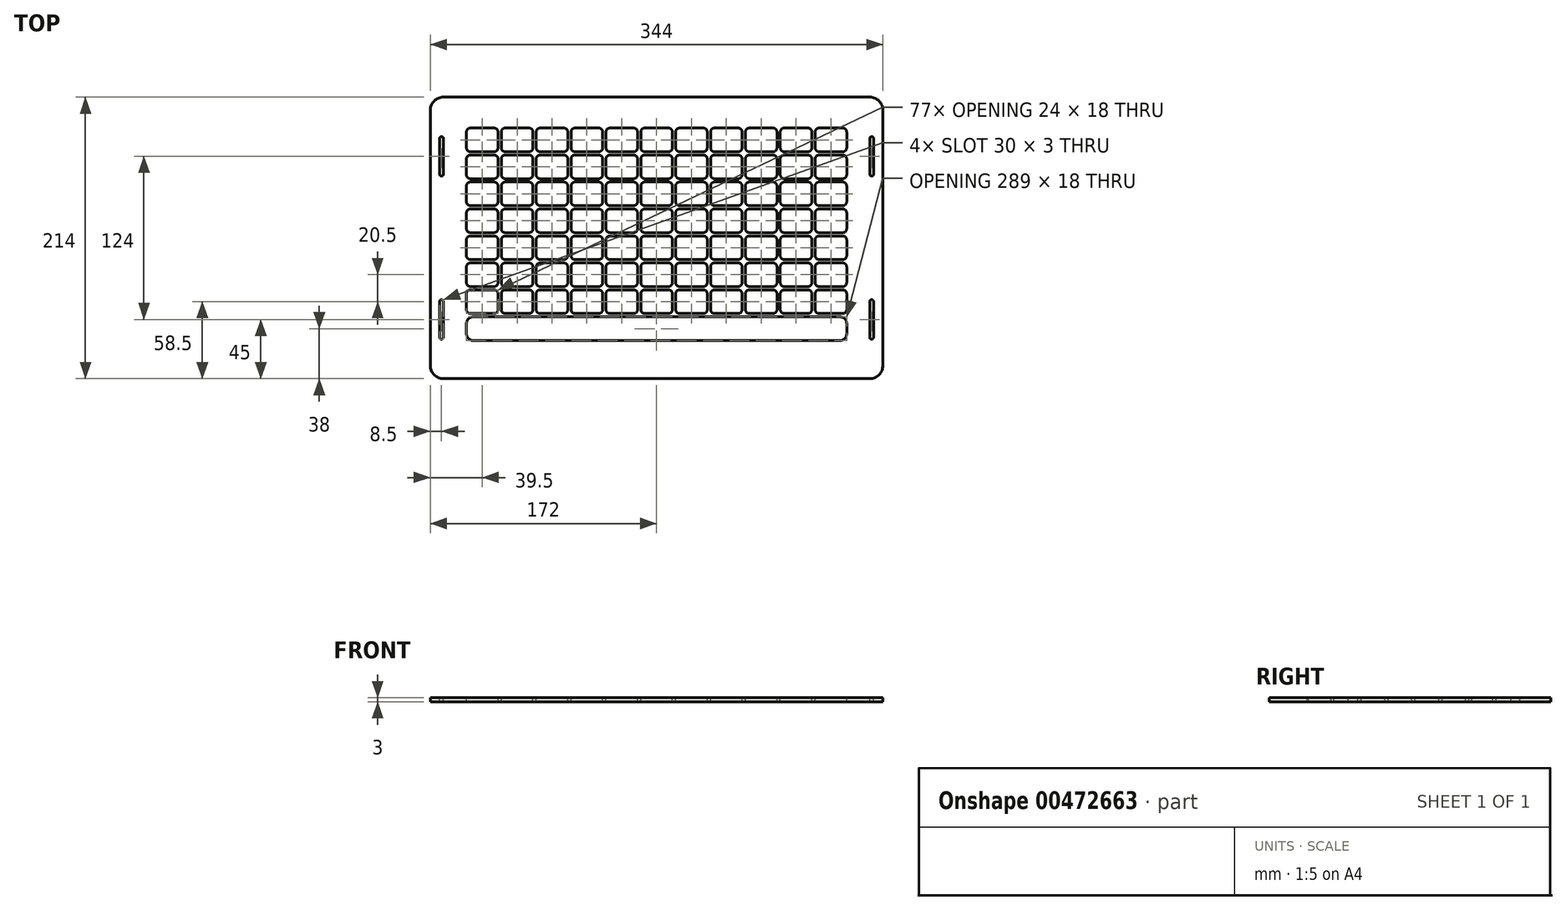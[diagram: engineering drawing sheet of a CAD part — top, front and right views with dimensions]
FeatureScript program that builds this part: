
annotation { "Feature Type Name" : "Feature", "Feature Type Description" : "" }
export const myFeature = defineFeature(function(context is Context, id is Id, definition is map)
    precondition{}
    {
        {
            var Q0;
            Q0=qCreatedBy(makeId("Top.planeOp"),FACE);
            var sketch = newSketch(context, id + "F0", { "sketchPlane" : qUnion([Q0])});
            skLineSegment(sketch, "E0.bottom", {"start": v(162, -107) * mm, "end": v(-162, -107) * mm});
            skLineSegment(sketch, "E0.top", {"start": v(162, 107) * mm, "end": v(-162, 107) * mm});
            skLineSegment(sketch, "E0.left", {"start": v(172, -97) * mm, "end": v(172, 97) * mm});
            skLineSegment(sketch, "E0.right", {"start": v(-172, -97) * mm, "end": v(-172, 97) * mm});
            skPoint(sketch, "E0.middle", {"position": v(0, 0) * mm});
            skPoint(sketch, "E1.visualSharp", {"position": v(-172, 107) * mm});
            skArc(sketch, "E1.filletArc", {"start": v(-162, 107) * mm, "mid": v(-169.07, 104.07) * mm, "end": v(-172, 97) * mm});
            skPoint(sketch, "E2.visualSharp", {"position": v(172, 107) * mm});
            skArc(sketch, "E2.filletArc", {"start": v(172, 97) * mm, "mid": v(169.07, 104.07) * mm, "end": v(162, 107) * mm});
            skPoint(sketch, "E3.visualSharp", {"position": v(172, -107) * mm});
            skArc(sketch, "E3.filletArc", {"start": v(162, -107) * mm, "mid": v(169.07, -104.07) * mm, "end": v(172, -97) * mm});
            skPoint(sketch, "E4.visualSharp", {"position": v(-172, -107) * mm});
            skArc(sketch, "E4.filletArc", {"start": v(-172, -97) * mm, "mid": v(-169.07, -104.07) * mm, "end": v(-162, -107) * mm});
            skSolve(sketch);
        }
        {
            var Q0;
            Q0 = qSketchRegion(id + "F0", true);
            extrude(context, id + "F1", {"entities" : qUnion([Q0]), "depth" : 3 * mm});
        }
        {
            var Q0;
            Q0=makeQuery(id+"F1.opExtrude","CAP_FACE",FACE,{"disambiguationData":[OSD([sQuery(id+"F0.wireOp",EDGE,"E0.bottom"),sQuery(id+"F0.wireOp",EDGE,"E0.top"),sQuery(id+"F0.wireOp",EDGE,"E0.left"),sQuery(id+"F0.wireOp",EDGE,"E0.right"),sQuery(id+"F0.wireOp",EDGE,"E1.filletArc"),sQuery(id+"F0.wireOp",EDGE,"E2.filletArc"),sQuery(id+"F0.wireOp",EDGE,"E3.filletArc"),sQuery(id+"F0.wireOp",EDGE,"E4.filletArc")])],"isStart":false});
            var sketch = newSketch(context, id + "F2", { "sketchPlane" : qUnion([Q0])});
            skLineSegment(sketch, "E5", {"start": v(-162, -47) * mm, "end": v(-162, -75.5) * mm});
            skLineSegment(sketch, "E6", {"start": v(0, 0) * mm, "end": v(72.85, 0) * mm, "construction": true});
            skLineSegment(sketch, "E7.bottom", {"start": v(-163.5, -77) * mm, "end": v(-163.5, -77) * mm});
            skLineSegment(sketch, "E7.top", {"start": v(-163.5, -47) * mm, "end": v(-163.5, -47) * mm});
            skLineSegment(sketch, "E7.left", {"start": v(-162, -77) * mm, "end": v(-162, -48.5) * mm});
            skLineSegment(sketch, "E7.right", {"start": v(-165, -75.5) * mm, "end": v(-165, -48.5) * mm});
            skPoint(sketch, "E8.visualSharp", {"position": v(-162, -47) * mm});
            skArc(sketch, "E8.filletArc", {"start": v(-162, -48.5) * mm, "mid": v(-162.44, -47.44) * mm, "end": v(-163.5, -47) * mm});
            skPoint(sketch, "E9.visualSharp", {"position": v(-165, -47) * mm});
            skArc(sketch, "E9.filletArc", {"start": v(-163.5, -47) * mm, "mid": v(-164.56, -47.44) * mm, "end": v(-165, -48.5) * mm});
            skPoint(sketch, "E10.visualSharp", {"position": v(-165, -77) * mm});
            skArc(sketch, "E10.filletArc", {"start": v(-165, -75.5) * mm, "mid": v(-164.56, -76.56) * mm, "end": v(-163.5, -77) * mm});
            skPoint(sketch, "E11.visualSharp", {"position": v(-162, -77) * mm});
            skArc(sketch, "E11.filletArc", {"start": v(-163.5, -77) * mm, "mid": v(-162.44, -76.56) * mm, "end": v(-162, -75.5) * mm});
            skPoint(sketch, "E12.end.orphan", {"position": v(-162, 77) * mm});
            skPoint(sketch, "E13.end.orphan", {"position": v(162, 77) * mm});
            skArc(sketch, "E14.MirrorCS", {"start": v(163.5, -77) * mm, "mid": v(162.44, -76.56) * mm, "end": v(162, -75.5) * mm});
            skArc(sketch, "E15.MirrorCS", {"start": v(165, -75.5) * mm, "mid": v(164.56, -76.56) * mm, "end": v(163.5, -77) * mm});
            skArc(sketch, "E16.MirrorCS", {"start": v(163.5, -47) * mm, "mid": v(164.56, -47.44) * mm, "end": v(165, -48.5) * mm});
            skArc(sketch, "E17.MirrorCS", {"start": v(162, -48.5) * mm, "mid": v(162.44, -47.44) * mm, "end": v(163.5, -47) * mm});
            skLineSegment(sketch, "E18.MirrorCS", {"start": v(162, -47) * mm, "end": v(162, -75.5) * mm});
            skLineSegment(sketch, "E19.MirrorCS", {"start": v(163.5, -77) * mm, "end": v(163.5, -77) * mm});
            skPoint(sketch, "E20.MirrorP", {"position": v(162, -47) * mm});
            skLineSegment(sketch, "E21.MirrorCS", {"start": v(163.5, -47) * mm, "end": v(163.5, -47) * mm});
            skLineSegment(sketch, "E22.MirrorCS", {"start": v(162, -77) * mm, "end": v(162, -48.5) * mm});
            skLineSegment(sketch, "E23.MirrorCS", {"start": v(165, -75.5) * mm, "end": v(165, -48.5) * mm});
            skPoint(sketch, "E24.MirrorP", {"position": v(165, -77) * mm});
            skPoint(sketch, "E25.MirrorP", {"position": v(165, -47) * mm});
            skPoint(sketch, "E26.MirrorP", {"position": v(162, -77) * mm});
            skArc(sketch, "E27.MirrorCS", {"start": v(-165, 75.5) * mm, "mid": v(-164.56, 76.56) * mm, "end": v(-163.5, 77) * mm});
            skArc(sketch, "E28.MirrorCS", {"start": v(-163.5, 77) * mm, "mid": v(-162.44, 76.56) * mm, "end": v(-162, 75.5) * mm});
            skArc(sketch, "E29.MirrorCS", {"start": v(165, 75.5) * mm, "mid": v(164.56, 76.56) * mm, "end": v(163.5, 77) * mm});
            skArc(sketch, "E30.MirrorCS", {"start": v(-162, 48.5) * mm, "mid": v(-162.44, 47.44) * mm, "end": v(-163.5, 47) * mm});
            skArc(sketch, "E31.MirrorCS", {"start": v(-163.5, 47) * mm, "mid": v(-164.56, 47.44) * mm, "end": v(-165, 48.5) * mm});
            skArc(sketch, "E32.MirrorCS", {"start": v(163.5, 77) * mm, "mid": v(162.44, 76.56) * mm, "end": v(162, 75.5) * mm});
            skArc(sketch, "E33.MirrorCS", {"start": v(163.5, 47) * mm, "mid": v(164.56, 47.44) * mm, "end": v(165, 48.5) * mm});
            skArc(sketch, "E34.MirrorCS", {"start": v(162, 48.5) * mm, "mid": v(162.44, 47.44) * mm, "end": v(163.5, 47) * mm});
            skLineSegment(sketch, "E35.MirrorCS", {"start": v(162, 47) * mm, "end": v(162, 75.5) * mm});
            skLineSegment(sketch, "E36.MirrorCS", {"start": v(-162, 47) * mm, "end": v(-162, 75.5) * mm});
            skPoint(sketch, "E37.MirrorP", {"position": v(162, 47) * mm});
            skLineSegment(sketch, "E38.MirrorCS", {"start": v(-162, 77) * mm, "end": v(-162, 48.5) * mm});
            skLineSegment(sketch, "E39.MirrorCS", {"start": v(-165, 75.5) * mm, "end": v(-165, 48.5) * mm});
            skLineSegment(sketch, "E40.MirrorCS", {"start": v(163.5, 47) * mm, "end": v(163.5, 47) * mm});
            skPoint(sketch, "E41.MirrorP", {"position": v(165, 77) * mm});
            skPoint(sketch, "E42.MirrorP", {"position": v(-165, 77) * mm});
            skPoint(sketch, "E43.MirrorP", {"position": v(165, 47) * mm});
            skLineSegment(sketch, "E44.MirrorCS", {"start": v(-163.5, 47) * mm, "end": v(-163.5, 47) * mm});
            skPoint(sketch, "E45.MirrorP", {"position": v(-162, 47) * mm});
            skLineSegment(sketch, "E46.MirrorCS", {"start": v(162, 77) * mm, "end": v(162, 48.5) * mm});
            skPoint(sketch, "E47.MirrorP", {"position": v(-165, 47) * mm});
            skLineSegment(sketch, "E48.MirrorCS", {"start": v(165, 75.5) * mm, "end": v(165, 48.5) * mm});
            skLineSegment(sketch, "E49.MirrorCS", {"start": v(163.5, 77) * mm, "end": v(163.5, 77) * mm});
            skLineSegment(sketch, "E50.MirrorCS", {"start": v(-163.5, 77) * mm, "end": v(-163.5, 77) * mm});
            skSolve(sketch);
        }
        {
            var Q0;
            Q0 = qSketchRegion(id + "F2", true);
            extrude(context, id + "F3", {"entities" : qUnion([Q0]), "operationType" : NewBodyOperationType.REMOVE, "oppositeDirection" : true, "depth" : 3 * mm});
        }
        {
            var Q0;
            Q0=makeQuery(id+"F1.opExtrude","CAP_FACE",FACE,{"disambiguationData":[OSD([sQuery(id+"F0.wireOp",EDGE,"E0.bottom"),sQuery(id+"F0.wireOp",EDGE,"E0.top"),sQuery(id+"F0.wireOp",EDGE,"E0.left"),sQuery(id+"F0.wireOp",EDGE,"E0.right"),sQuery(id+"F0.wireOp",EDGE,"E1.filletArc"),sQuery(id+"F0.wireOp",EDGE,"E2.filletArc"),sQuery(id+"F0.wireOp",EDGE,"E3.filletArc"),sQuery(id+"F0.wireOp",EDGE,"E4.filletArc")])],"isStart":false});
            var sketch = newSketch(context, id + "F4", { "sketchPlane" : qUnion([Q0])});
            skLineSegment(sketch, "E51.top", {"start": v(-9, 4) * mm, "end": v(9, 4) * mm});
            skLineSegment(sketch, "E51.left", {"start": v(-12, 19) * mm, "end": v(-12, 7) * mm});
            skLineSegment(sketch, "E51.right", {"start": v(12, 19) * mm, "end": v(12, 7) * mm});
            skPoint(sketch, "E51.middle", {"position": v(0, 13) * mm});
            skPoint(sketch, "E52.visualSharp", {"position": v(-12, 22) * mm});
            skArc(sketch, "E52.filletArc", {"start": v(-9, 22) * mm, "mid": v(-11.12, 21.12) * mm, "end": v(-12, 19) * mm});
            skPoint(sketch, "E53.visualSharp", {"position": v(12, 22) * mm});
            skArc(sketch, "E53.filletArc", {"start": v(12, 19) * mm, "mid": v(11.12, 21.12) * mm, "end": v(9, 22) * mm});
            skPoint(sketch, "E54.visualSharp", {"position": v(12, 4) * mm});
            skArc(sketch, "E54.filletArc", {"start": v(9, 4) * mm, "mid": v(11.12, 4.88) * mm, "end": v(12, 7) * mm});
            skPoint(sketch, "E55.visualSharp", {"position": v(-12, 4) * mm});
            skArc(sketch, "E55.filletArc", {"start": v(-12, 7) * mm, "mid": v(-11.12, 4.88) * mm, "end": v(-9, 4) * mm});
            skPoint(sketch, "E56.1.0.0", {"position": v(14.5, 4) * mm});
            skPoint(sketch, "E56.1.0.1", {"position": v(38.5, 4) * mm});
            skPoint(sketch, "E56.1.0.2", {"position": v(26.5, 13) * mm});
            skLineSegment(sketch, "E56.1.0.3", {"start": v(38.5, 19) * mm, "end": v(38.5, 7) * mm});
            skLineSegment(sketch, "E56.1.0.4", {"start": v(14.5, 19) * mm, "end": v(14.5, 7) * mm});
            skPoint(sketch, "E56.1.0.5", {"position": v(38.5, 22) * mm});
            skPoint(sketch, "E56.1.0.6", {"position": v(14.5, 22) * mm});
            skLineSegment(sketch, "E56.1.0.7", {"start": v(17.5, 22) * mm, "end": v(35.5, 22) * mm});
            skLineSegment(sketch, "E56.1.0.8", {"start": v(17.5, 4) * mm, "end": v(35.5, 4) * mm});
            skArc(sketch, "E56.1.0.9", {"start": v(14.5, 7) * mm, "mid": v(15.38, 4.88) * mm, "end": v(17.5, 4) * mm});
            skArc(sketch, "E56.1.0.10", {"start": v(35.5, 4) * mm, "mid": v(37.62, 4.88) * mm, "end": v(38.5, 7) * mm});
            skArc(sketch, "E56.1.0.11", {"start": v(38.5, 19) * mm, "mid": v(37.62, 21.12) * mm, "end": v(35.5, 22) * mm});
            skArc(sketch, "E56.1.0.12", {"start": v(17.5, 22) * mm, "mid": v(15.38, 21.12) * mm, "end": v(14.5, 19) * mm});
            skPoint(sketch, "E56.2.0.0", {"position": v(41, 4) * mm});
            skPoint(sketch, "E56.2.0.1", {"position": v(65, 4) * mm});
            skPoint(sketch, "E56.2.0.2", {"position": v(53, 13) * mm});
            skLineSegment(sketch, "E56.2.0.3", {"start": v(65, 19) * mm, "end": v(65, 7) * mm});
            skLineSegment(sketch, "E56.2.0.4", {"start": v(41, 19) * mm, "end": v(41, 7) * mm});
            skPoint(sketch, "E56.2.0.5", {"position": v(65, 22) * mm});
            skPoint(sketch, "E56.2.0.6", {"position": v(41, 22) * mm});
            skLineSegment(sketch, "E56.2.0.7", {"start": v(44, 22) * mm, "end": v(62, 22) * mm});
            skLineSegment(sketch, "E56.2.0.8", {"start": v(44, 4) * mm, "end": v(62, 4) * mm});
            skArc(sketch, "E56.2.0.9", {"start": v(41, 7) * mm, "mid": v(41.88, 4.88) * mm, "end": v(44, 4) * mm});
            skArc(sketch, "E56.2.0.10", {"start": v(62, 4) * mm, "mid": v(64.12, 4.88) * mm, "end": v(65, 7) * mm});
            skArc(sketch, "E56.2.0.11", {"start": v(65, 19) * mm, "mid": v(64.12, 21.12) * mm, "end": v(62, 22) * mm});
            skArc(sketch, "E56.2.0.12", {"start": v(44, 22) * mm, "mid": v(41.88, 21.12) * mm, "end": v(41, 19) * mm});
            skPoint(sketch, "E56.3.0.0", {"position": v(67.5, 4) * mm});
            skPoint(sketch, "E56.3.0.1", {"position": v(91.5, 4) * mm});
            skPoint(sketch, "E56.3.0.2", {"position": v(79.5, 13) * mm});
            skLineSegment(sketch, "E56.3.0.3", {"start": v(91.5, 19) * mm, "end": v(91.5, 7) * mm});
            skLineSegment(sketch, "E56.3.0.4", {"start": v(67.5, 19) * mm, "end": v(67.5, 7) * mm});
            skPoint(sketch, "E56.3.0.5", {"position": v(91.5, 22) * mm});
            skPoint(sketch, "E56.3.0.6", {"position": v(67.5, 22) * mm});
            skLineSegment(sketch, "E56.3.0.7", {"start": v(70.5, 22) * mm, "end": v(88.5, 22) * mm});
            skLineSegment(sketch, "E56.3.0.8", {"start": v(70.5, 4) * mm, "end": v(88.5, 4) * mm});
            skArc(sketch, "E56.3.0.9", {"start": v(67.5, 7) * mm, "mid": v(68.38, 4.88) * mm, "end": v(70.5, 4) * mm});
            skArc(sketch, "E56.3.0.10", {"start": v(88.5, 4) * mm, "mid": v(90.62, 4.88) * mm, "end": v(91.5, 7) * mm});
            skArc(sketch, "E56.3.0.11", {"start": v(91.5, 19) * mm, "mid": v(90.62, 21.12) * mm, "end": v(88.5, 22) * mm});
            skArc(sketch, "E56.3.0.12", {"start": v(70.5, 22) * mm, "mid": v(68.38, 21.12) * mm, "end": v(67.5, 19) * mm});
            skPoint(sketch, "E56.4.0.0", {"position": v(94, 4) * mm});
            skPoint(sketch, "E56.4.0.1", {"position": v(118, 4) * mm});
            skPoint(sketch, "E56.4.0.2", {"position": v(106, 13) * mm});
            skLineSegment(sketch, "E56.4.0.3", {"start": v(118, 19) * mm, "end": v(118, 7) * mm});
            skLineSegment(sketch, "E56.4.0.4", {"start": v(94, 19) * mm, "end": v(94, 7) * mm});
            skPoint(sketch, "E56.4.0.5", {"position": v(118, 22) * mm});
            skPoint(sketch, "E56.4.0.6", {"position": v(94, 22) * mm});
            skLineSegment(sketch, "E56.4.0.7", {"start": v(97, 22) * mm, "end": v(115, 22) * mm});
            skLineSegment(sketch, "E56.4.0.8", {"start": v(97, 4) * mm, "end": v(115, 4) * mm});
            skArc(sketch, "E56.4.0.9", {"start": v(94, 7) * mm, "mid": v(94.88, 4.88) * mm, "end": v(97, 4) * mm});
            skArc(sketch, "E56.4.0.10", {"start": v(115, 4) * mm, "mid": v(117.12, 4.88) * mm, "end": v(118, 7) * mm});
            skArc(sketch, "E56.4.0.11", {"start": v(118, 19) * mm, "mid": v(117.12, 21.12) * mm, "end": v(115, 22) * mm});
            skArc(sketch, "E56.4.0.12", {"start": v(97, 22) * mm, "mid": v(94.88, 21.12) * mm, "end": v(94, 19) * mm});
            skPoint(sketch, "E56.5.0.0", {"position": v(120.5, 4) * mm});
            skPoint(sketch, "E56.5.0.1", {"position": v(144.5, 4) * mm});
            skPoint(sketch, "E56.5.0.2", {"position": v(132.5, 13) * mm});
            skLineSegment(sketch, "E56.5.0.3", {"start": v(144.5, 19) * mm, "end": v(144.5, 7) * mm});
            skLineSegment(sketch, "E56.5.0.4", {"start": v(120.5, 19) * mm, "end": v(120.5, 7) * mm});
            skPoint(sketch, "E56.5.0.5", {"position": v(144.5, 22) * mm});
            skPoint(sketch, "E56.5.0.6", {"position": v(120.5, 22) * mm});
            skLineSegment(sketch, "E56.5.0.7", {"start": v(123.5, 22) * mm, "end": v(141.5, 22) * mm});
            skLineSegment(sketch, "E56.5.0.8", {"start": v(123.5, 4) * mm, "end": v(141.5, 4) * mm});
            skArc(sketch, "E56.5.0.9", {"start": v(120.5, 7) * mm, "mid": v(121.38, 4.88) * mm, "end": v(123.5, 4) * mm});
            skArc(sketch, "E56.5.0.10", {"start": v(141.5, 4) * mm, "mid": v(143.62, 4.88) * mm, "end": v(144.5, 7) * mm});
            skArc(sketch, "E56.5.0.11", {"start": v(144.5, 19) * mm, "mid": v(143.62, 21.12) * mm, "end": v(141.5, 22) * mm});
            skArc(sketch, "E56.5.0.12", {"start": v(123.5, 22) * mm, "mid": v(121.38, 21.12) * mm, "end": v(120.5, 19) * mm});
            skLineSegment(sketch, "E56.direction1", {"start": v(-12, 4) * mm, "end": v(14.5, 4) * mm, "construction": true});
            skLineSegment(sketch, "E57.1.0.0", {"start": v(-14.5, 19) * mm, "end": v(-14.5, 7) * mm});
            skLineSegment(sketch, "E57.1.0.1", {"start": v(-38.5, 19) * mm, "end": v(-38.5, 7) * mm});
            skLineSegment(sketch, "E57.1.0.2", {"start": v(-35.5, 4) * mm, "end": v(-17.5, 4) * mm});
            skLineSegment(sketch, "E57.1.0.3", {"start": v(-35.5, 22) * mm, "end": v(-17.5, 22) * mm});
            skPoint(sketch, "E57.1.0.4", {"position": v(-38.5, 22) * mm});
            skPoint(sketch, "E57.1.0.5", {"position": v(-26.5, 13) * mm});
            skPoint(sketch, "E57.1.0.6", {"position": v(-38.5, 4) * mm});
            skPoint(sketch, "E57.1.0.7", {"position": v(-14.5, 4) * mm});
            skPoint(sketch, "E57.1.0.8", {"position": v(-14.5, 22) * mm});
            skArc(sketch, "E57.1.0.9", {"start": v(-17.5, 4) * mm, "mid": v(-15.38, 4.88) * mm, "end": v(-14.5, 7) * mm});
            skArc(sketch, "E57.1.0.10", {"start": v(-14.5, 19) * mm, "mid": v(-15.38, 21.12) * mm, "end": v(-17.5, 22) * mm});
            skArc(sketch, "E57.1.0.11", {"start": v(-35.5, 22) * mm, "mid": v(-37.62, 21.12) * mm, "end": v(-38.5, 19) * mm});
            skArc(sketch, "E57.1.0.12", {"start": v(-38.5, 7) * mm, "mid": v(-37.62, 4.88) * mm, "end": v(-35.5, 4) * mm});
            skLineSegment(sketch, "E57.2.0.0", {"start": v(-41, 19) * mm, "end": v(-41, 7) * mm});
            skLineSegment(sketch, "E57.2.0.1", {"start": v(-65, 19) * mm, "end": v(-65, 7) * mm});
            skLineSegment(sketch, "E57.2.0.2", {"start": v(-62, 4) * mm, "end": v(-44, 4) * mm});
            skLineSegment(sketch, "E57.2.0.3", {"start": v(-62, 22) * mm, "end": v(-44, 22) * mm});
            skPoint(sketch, "E57.2.0.4", {"position": v(-65, 22) * mm});
            skPoint(sketch, "E57.2.0.5", {"position": v(-53, 13) * mm});
            skPoint(sketch, "E57.2.0.6", {"position": v(-65, 4) * mm});
            skPoint(sketch, "E57.2.0.7", {"position": v(-41, 4) * mm});
            skPoint(sketch, "E57.2.0.8", {"position": v(-41, 22) * mm});
            skArc(sketch, "E57.2.0.9", {"start": v(-44, 4) * mm, "mid": v(-41.88, 4.88) * mm, "end": v(-41, 7) * mm});
            skArc(sketch, "E57.2.0.10", {"start": v(-41, 19) * mm, "mid": v(-41.88, 21.12) * mm, "end": v(-44, 22) * mm});
            skArc(sketch, "E57.2.0.11", {"start": v(-62, 22) * mm, "mid": v(-64.12, 21.12) * mm, "end": v(-65, 19) * mm});
            skArc(sketch, "E57.2.0.12", {"start": v(-65, 7) * mm, "mid": v(-64.12, 4.88) * mm, "end": v(-62, 4) * mm});
            skLineSegment(sketch, "E57.3.0.0", {"start": v(-67.5, 19) * mm, "end": v(-67.5, 7) * mm});
            skLineSegment(sketch, "E57.3.0.1", {"start": v(-91.5, 19) * mm, "end": v(-91.5, 7) * mm});
            skLineSegment(sketch, "E57.3.0.2", {"start": v(-88.5, 4) * mm, "end": v(-70.5, 4) * mm});
            skLineSegment(sketch, "E57.3.0.3", {"start": v(-88.5, 22) * mm, "end": v(-70.5, 22) * mm});
            skPoint(sketch, "E57.3.0.4", {"position": v(-91.5, 22) * mm});
            skPoint(sketch, "E57.3.0.5", {"position": v(-79.5, 13) * mm});
            skPoint(sketch, "E57.3.0.6", {"position": v(-91.5, 4) * mm});
            skPoint(sketch, "E57.3.0.7", {"position": v(-67.5, 4) * mm});
            skPoint(sketch, "E57.3.0.8", {"position": v(-67.5, 22) * mm});
            skArc(sketch, "E57.3.0.9", {"start": v(-70.5, 4) * mm, "mid": v(-68.38, 4.88) * mm, "end": v(-67.5, 7) * mm});
            skArc(sketch, "E57.3.0.10", {"start": v(-67.5, 19) * mm, "mid": v(-68.38, 21.12) * mm, "end": v(-70.5, 22) * mm});
            skArc(sketch, "E57.3.0.11", {"start": v(-88.5, 22) * mm, "mid": v(-90.62, 21.12) * mm, "end": v(-91.5, 19) * mm});
            skArc(sketch, "E57.3.0.12", {"start": v(-91.5, 7) * mm, "mid": v(-90.62, 4.88) * mm, "end": v(-88.5, 4) * mm});
            skLineSegment(sketch, "E57.4.0.0", {"start": v(-94, 19) * mm, "end": v(-94, 7) * mm});
            skLineSegment(sketch, "E57.4.0.1", {"start": v(-118, 19) * mm, "end": v(-118, 7) * mm});
            skLineSegment(sketch, "E57.4.0.2", {"start": v(-115, 4) * mm, "end": v(-97, 4) * mm});
            skLineSegment(sketch, "E57.4.0.3", {"start": v(-115, 22) * mm, "end": v(-97, 22) * mm});
            skPoint(sketch, "E57.4.0.4", {"position": v(-118, 22) * mm});
            skPoint(sketch, "E57.4.0.5", {"position": v(-106, 13) * mm});
            skPoint(sketch, "E57.4.0.6", {"position": v(-118, 4) * mm});
            skPoint(sketch, "E57.4.0.7", {"position": v(-94, 4) * mm});
            skPoint(sketch, "E57.4.0.8", {"position": v(-94, 22) * mm});
            skArc(sketch, "E57.4.0.9", {"start": v(-97, 4) * mm, "mid": v(-94.88, 4.88) * mm, "end": v(-94, 7) * mm});
            skArc(sketch, "E57.4.0.10", {"start": v(-94, 19) * mm, "mid": v(-94.88, 21.12) * mm, "end": v(-97, 22) * mm});
            skArc(sketch, "E57.4.0.11", {"start": v(-115, 22) * mm, "mid": v(-117.12, 21.12) * mm, "end": v(-118, 19) * mm});
            skArc(sketch, "E57.4.0.12", {"start": v(-118, 7) * mm, "mid": v(-117.12, 4.88) * mm, "end": v(-115, 4) * mm});
            skLineSegment(sketch, "E57.5.0.0", {"start": v(-120.5, 19) * mm, "end": v(-120.5, 7) * mm});
            skLineSegment(sketch, "E57.5.0.1", {"start": v(-144.5, 19) * mm, "end": v(-144.5, 7) * mm});
            skLineSegment(sketch, "E57.5.0.2", {"start": v(-141.5, 4) * mm, "end": v(-123.5, 4) * mm});
            skLineSegment(sketch, "E57.5.0.3", {"start": v(-141.5, 22) * mm, "end": v(-123.5, 22) * mm});
            skPoint(sketch, "E57.5.0.4", {"position": v(-144.5, 22) * mm});
            skPoint(sketch, "E57.5.0.5", {"position": v(-132.5, 13) * mm});
            skPoint(sketch, "E57.5.0.6", {"position": v(-144.5, 4) * mm});
            skPoint(sketch, "E57.5.0.7", {"position": v(-120.5, 4) * mm});
            skPoint(sketch, "E57.5.0.8", {"position": v(-120.5, 22) * mm});
            skArc(sketch, "E57.5.0.9", {"start": v(-123.5, 4) * mm, "mid": v(-121.38, 4.88) * mm, "end": v(-120.5, 7) * mm});
            skArc(sketch, "E57.5.0.10", {"start": v(-120.5, 19) * mm, "mid": v(-121.38, 21.12) * mm, "end": v(-123.5, 22) * mm});
            skArc(sketch, "E57.5.0.11", {"start": v(-141.5, 22) * mm, "mid": v(-143.62, 21.12) * mm, "end": v(-144.5, 19) * mm});
            skArc(sketch, "E57.5.0.12", {"start": v(-144.5, 7) * mm, "mid": v(-143.62, 4.88) * mm, "end": v(-141.5, 4) * mm});
            skLineSegment(sketch, "E57.direction1", {"start": v(-12, 4) * mm, "end": v(-38.5, 4) * mm, "construction": true});
            skPoint(sketch, "E58.0.1.0", {"position": v(41, 42.5) * mm});
            skPoint(sketch, "E58.0.1.1", {"position": v(106, 33.5) * mm});
            skPoint(sketch, "E58.0.1.2", {"position": v(-38.5, 42.5) * mm});
            skLineSegment(sketch, "E58.0.1.3", {"start": v(-9, 42.5) * mm, "end": v(9, 42.5) * mm});
            skPoint(sketch, "E58.0.1.5", {"position": v(-94, 42.5) * mm});
            skPoint(sketch, "E58.0.1.6", {"position": v(65, 42.5) * mm});
            skPoint(sketch, "E58.0.1.7", {"position": v(118, 24.5) * mm});
            skPoint(sketch, "E58.0.1.8", {"position": v(12, 24.5) * mm});
            skPoint(sketch, "E58.0.1.9", {"position": v(-94, 24.5) * mm});
            skPoint(sketch, "E58.0.1.10", {"position": v(53, 33.5) * mm});
            skPoint(sketch, "E58.0.1.11", {"position": v(94, 24.5) * mm});
            skPoint(sketch, "E58.0.1.12", {"position": v(65, 24.5) * mm});
            skPoint(sketch, "E58.0.1.13", {"position": v(-118, 24.5) * mm});
            skPoint(sketch, "E58.0.1.14", {"position": v(-41, 42.5) * mm});
            skPoint(sketch, "E58.0.1.15", {"position": v(12, 42.5) * mm});
            skLineSegment(sketch, "E58.0.1.16", {"start": v(-62, 42.5) * mm, "end": v(-44, 42.5) * mm});
            skLineSegment(sketch, "E58.0.1.17", {"start": v(-115, 42.5) * mm, "end": v(-97, 42.5) * mm});
            skPoint(sketch, "E58.0.1.18", {"position": v(-106, 33.5) * mm});
            skPoint(sketch, "E58.0.1.19", {"position": v(41, 24.5) * mm});
            skPoint(sketch, "E58.0.1.20", {"position": v(-41, 24.5) * mm});
            skLineSegment(sketch, "E58.0.1.21", {"start": v(17.5, 24.5) * mm, "end": v(35.5, 24.5) * mm});
            skPoint(sketch, "E58.0.1.22", {"position": v(-118, 42.5) * mm});
            skPoint(sketch, "E58.0.1.23", {"position": v(120.5, 42.5) * mm});
            skPoint(sketch, "E58.0.1.24", {"position": v(-65, 24.5) * mm});
            skPoint(sketch, "E58.0.1.25", {"position": v(-12, 42.5) * mm});
            skPoint(sketch, "E58.0.1.26", {"position": v(67.5, 24.5) * mm});
            skPoint(sketch, "E58.0.1.27", {"position": v(26.5, 33.5) * mm});
            skPoint(sketch, "E58.0.1.28", {"position": v(118, 42.5) * mm});
            skPoint(sketch, "E58.0.1.29", {"position": v(-12, 24.5) * mm});
            skPoint(sketch, "E58.0.1.30", {"position": v(-26.5, 33.5) * mm});
            skPoint(sketch, "E58.0.1.31", {"position": v(94, 42.5) * mm});
            skPoint(sketch, "E58.0.1.32", {"position": v(-91.5, 42.5) * mm});
            skPoint(sketch, "E58.0.1.33", {"position": v(-38.5, 24.5) * mm});
            skLineSegment(sketch, "E58.0.1.34", {"start": v(44, 42.5) * mm, "end": v(62, 42.5) * mm});
            skLineSegment(sketch, "E58.0.1.35", {"start": v(97, 42.5) * mm, "end": v(115, 42.5) * mm});
            skPoint(sketch, "E58.0.1.36", {"position": v(144.5, 24.5) * mm});
            skPoint(sketch, "E58.0.1.37", {"position": v(91.5, 42.5) * mm});
            skPoint(sketch, "E58.0.1.38", {"position": v(14.5, 24.5) * mm});
            skPoint(sketch, "E58.0.1.39", {"position": v(-79.5, 33.5) * mm});
            skPoint(sketch, "E58.0.1.40", {"position": v(-14.5, 24.5) * mm});
            skLineSegment(sketch, "E58.0.1.41", {"start": v(97, 24.5) * mm, "end": v(115, 24.5) * mm});
            skPoint(sketch, "E58.0.1.42", {"position": v(-120.5, 42.5) * mm});
            skLineSegment(sketch, "E58.0.1.43", {"start": v(-141.5, 24.5) * mm, "end": v(-123.5, 24.5) * mm});
            skLineSegment(sketch, "E58.0.1.44", {"start": v(44, 24.5) * mm, "end": v(62, 24.5) * mm});
            skLineSegment(sketch, "E58.0.1.45", {"start": v(-88.5, 24.5) * mm, "end": v(-70.5, 24.5) * mm});
            skPoint(sketch, "E58.0.1.46", {"position": v(91.5, 24.5) * mm});
            skPoint(sketch, "E58.0.1.47", {"position": v(38.5, 42.5) * mm});
            skPoint(sketch, "E58.0.1.48", {"position": v(-67.5, 42.5) * mm});
            skPoint(sketch, "E58.0.1.49", {"position": v(-144.5, 24.5) * mm});
            skPoint(sketch, "E58.0.1.50", {"position": v(38.5, 24.5) * mm});
            skPoint(sketch, "E58.0.1.51", {"position": v(-91.5, 24.5) * mm});
            skPoint(sketch, "E58.0.1.52", {"position": v(-144.5, 42.5) * mm});
            skPoint(sketch, "E58.0.1.53", {"position": v(-14.5, 42.5) * mm});
            skLineSegment(sketch, "E58.0.1.54", {"start": v(-35.5, 42.5) * mm, "end": v(-17.5, 42.5) * mm});
            skLineSegment(sketch, "E58.0.1.55", {"start": v(-141.5, 42.5) * mm, "end": v(-123.5, 42.5) * mm});
            skPoint(sketch, "E58.0.1.56", {"position": v(-65, 42.5) * mm});
            skLineSegment(sketch, "E58.0.1.57", {"start": v(-88.5, 42.5) * mm, "end": v(-70.5, 42.5) * mm});
            skPoint(sketch, "E58.0.1.58", {"position": v(67.5, 42.5) * mm});
            skPoint(sketch, "E58.0.1.59", {"position": v(132.5, 33.5) * mm});
            skLineSegment(sketch, "E58.0.1.60", {"start": v(-12, 24.5) * mm, "end": v(-38.5, 24.5) * mm, "construction": true});
            skLineSegment(sketch, "E58.0.1.61", {"start": v(17.5, 42.5) * mm, "end": v(35.5, 42.5) * mm});
            skPoint(sketch, "E58.0.1.62", {"position": v(79.5, 33.5) * mm});
            skPoint(sketch, "E58.0.1.63", {"position": v(14.5, 42.5) * mm});
            skPoint(sketch, "E58.0.1.64", {"position": v(-120.5, 24.5) * mm});
            skPoint(sketch, "E58.0.1.65", {"position": v(-132.5, 33.5) * mm});
            skPoint(sketch, "E58.0.1.66", {"position": v(-67.5, 24.5) * mm});
            skPoint(sketch, "E58.0.1.67", {"position": v(0, 33.5) * mm});
            skPoint(sketch, "E58.0.1.68", {"position": v(120.5, 24.5) * mm});
            skLineSegment(sketch, "E58.0.1.69", {"start": v(70.5, 42.5) * mm, "end": v(88.5, 42.5) * mm});
            skLineSegment(sketch, "E58.0.1.70", {"start": v(123.5, 42.5) * mm, "end": v(141.5, 42.5) * mm});
            skLineSegment(sketch, "E58.0.1.71", {"start": v(70.5, 24.5) * mm, "end": v(88.5, 24.5) * mm});
            skLineSegment(sketch, "E58.0.1.72", {"start": v(123.5, 24.5) * mm, "end": v(141.5, 24.5) * mm});
            skLineSegment(sketch, "E58.0.1.73", {"start": v(-115, 24.5) * mm, "end": v(-97, 24.5) * mm});
            skPoint(sketch, "E58.0.1.74", {"position": v(-53, 33.5) * mm});
            skPoint(sketch, "E58.0.1.75", {"position": v(144.5, 42.5) * mm});
            skLineSegment(sketch, "E58.0.1.76", {"start": v(-62, 24.5) * mm, "end": v(-44, 24.5) * mm});
            skLineSegment(sketch, "E58.0.1.77", {"start": v(118, 39.5) * mm, "end": v(118, 27.5) * mm});
            skLineSegment(sketch, "E58.0.1.78", {"start": v(-12, 24.5) * mm, "end": v(14.5, 24.5) * mm, "construction": true});
            skLineSegment(sketch, "E58.0.1.79", {"start": v(65, 39.5) * mm, "end": v(65, 27.5) * mm});
            skLineSegment(sketch, "E58.0.1.80", {"start": v(12, 39.5) * mm, "end": v(12, 27.5) * mm});
            skLineSegment(sketch, "E58.0.1.81", {"start": v(-12, 39.5) * mm, "end": v(-12, 27.5) * mm});
            skLineSegment(sketch, "E58.0.1.82", {"start": v(14.5, 39.5) * mm, "end": v(14.5, 27.5) * mm});
            skLineSegment(sketch, "E58.0.1.83", {"start": v(38.5, 39.5) * mm, "end": v(38.5, 27.5) * mm});
            skLineSegment(sketch, "E58.0.1.84", {"start": v(-14.5, 39.5) * mm, "end": v(-14.5, 27.5) * mm});
            skLineSegment(sketch, "E58.0.1.85", {"start": v(94, 39.5) * mm, "end": v(94, 27.5) * mm});
            skLineSegment(sketch, "E58.0.1.86", {"start": v(41, 39.5) * mm, "end": v(41, 27.5) * mm});
            skLineSegment(sketch, "E58.0.1.87", {"start": v(-120.5, 39.5) * mm, "end": v(-120.5, 27.5) * mm});
            skLineSegment(sketch, "E58.0.1.88", {"start": v(-67.5, 39.5) * mm, "end": v(-67.5, 27.5) * mm});
            skLineSegment(sketch, "E58.0.1.89", {"start": v(-38.5, 39.5) * mm, "end": v(-38.5, 27.5) * mm});
            skLineSegment(sketch, "E58.0.1.90", {"start": v(-144.5, 39.5) * mm, "end": v(-144.5, 27.5) * mm});
            skLineSegment(sketch, "E58.0.1.91", {"start": v(-91.5, 39.5) * mm, "end": v(-91.5, 27.5) * mm});
            skLineSegment(sketch, "E58.0.1.92", {"start": v(-35.5, 24.5) * mm, "end": v(-17.5, 24.5) * mm});
            skLineSegment(sketch, "E58.0.1.93", {"start": v(144.5, 39.5) * mm, "end": v(144.5, 27.5) * mm});
            skLineSegment(sketch, "E58.0.1.94", {"start": v(91.5, 39.5) * mm, "end": v(91.5, 27.5) * mm});
            skLineSegment(sketch, "E58.0.1.95", {"start": v(-94, 39.5) * mm, "end": v(-94, 27.5) * mm});
            skLineSegment(sketch, "E58.0.1.96", {"start": v(-41, 39.5) * mm, "end": v(-41, 27.5) * mm});
            skLineSegment(sketch, "E58.0.1.97", {"start": v(120.5, 39.5) * mm, "end": v(120.5, 27.5) * mm});
            skLineSegment(sketch, "E58.0.1.98", {"start": v(67.5, 39.5) * mm, "end": v(67.5, 27.5) * mm});
            skLineSegment(sketch, "E58.0.1.99", {"start": v(-118, 39.5) * mm, "end": v(-118, 27.5) * mm});
            skLineSegment(sketch, "E58.0.1.100", {"start": v(-65, 39.5) * mm, "end": v(-65, 27.5) * mm});
            skArc(sketch, "E58.0.1.101", {"start": v(-65, 27.5) * mm, "mid": v(-64.12, 25.38) * mm, "end": v(-62, 24.5) * mm});
            skArc(sketch, "E58.0.1.102", {"start": v(-118, 27.5) * mm, "mid": v(-117.12, 25.38) * mm, "end": v(-115, 24.5) * mm});
            skArc(sketch, "E58.0.1.103", {"start": v(12, 39.5) * mm, "mid": v(11.12, 41.62) * mm, "end": v(9, 42.5) * mm});
            skArc(sketch, "E58.0.1.104", {"start": v(-9, 42.5) * mm, "mid": v(-11.12, 41.62) * mm, "end": v(-12, 39.5) * mm});
            skLineSegment(sketch, "E58.0.1.105", {"start": v(-9, 24.5) * mm, "end": v(9, 24.5) * mm});
            skArc(sketch, "E58.0.1.106", {"start": v(-62, 42.5) * mm, "mid": v(-64.12, 41.62) * mm, "end": v(-65, 39.5) * mm});
            skArc(sketch, "E58.0.1.107", {"start": v(-115, 42.5) * mm, "mid": v(-117.12, 41.62) * mm, "end": v(-118, 39.5) * mm});
            skArc(sketch, "E58.0.1.108", {"start": v(-94, 39.5) * mm, "mid": v(-94.88, 41.62) * mm, "end": v(-97, 42.5) * mm});
            skArc(sketch, "E58.0.1.109", {"start": v(38.5, 39.5) * mm, "mid": v(37.62, 41.62) * mm, "end": v(35.5, 42.5) * mm});
            skArc(sketch, "E58.0.1.110", {"start": v(67.5, 27.5) * mm, "mid": v(68.38, 25.38) * mm, "end": v(70.5, 24.5) * mm});
            skArc(sketch, "E58.0.1.111", {"start": v(120.5, 27.5) * mm, "mid": v(121.38, 25.38) * mm, "end": v(123.5, 24.5) * mm});
            skArc(sketch, "E58.0.1.112", {"start": v(14.5, 27.5) * mm, "mid": v(15.38, 25.38) * mm, "end": v(17.5, 24.5) * mm});
            skArc(sketch, "E58.0.1.113", {"start": v(65, 39.5) * mm, "mid": v(64.12, 41.62) * mm, "end": v(62, 42.5) * mm});
            skArc(sketch, "E58.0.1.114", {"start": v(118, 39.5) * mm, "mid": v(117.12, 41.62) * mm, "end": v(115, 42.5) * mm});
            skArc(sketch, "E58.0.1.115", {"start": v(-91.5, 27.5) * mm, "mid": v(-90.62, 25.38) * mm, "end": v(-88.5, 24.5) * mm});
            skArc(sketch, "E58.0.1.116", {"start": v(-38.5, 27.5) * mm, "mid": v(-37.62, 25.38) * mm, "end": v(-35.5, 24.5) * mm});
            skArc(sketch, "E58.0.1.117", {"start": v(94, 27.5) * mm, "mid": v(94.88, 25.38) * mm, "end": v(97, 24.5) * mm});
            skArc(sketch, "E58.0.1.118", {"start": v(41, 27.5) * mm, "mid": v(41.88, 25.38) * mm, "end": v(44, 24.5) * mm});
            skArc(sketch, "E58.0.1.119", {"start": v(115, 24.5) * mm, "mid": v(117.12, 25.38) * mm, "end": v(118, 27.5) * mm});
            skArc(sketch, "E58.0.1.120", {"start": v(62, 24.5) * mm, "mid": v(64.12, 25.38) * mm, "end": v(65, 27.5) * mm});
            skArc(sketch, "E58.0.1.121", {"start": v(44, 42.5) * mm, "mid": v(41.88, 41.62) * mm, "end": v(41, 39.5) * mm});
            skArc(sketch, "E58.0.1.122", {"start": v(-17.5, 24.5) * mm, "mid": v(-15.38, 25.38) * mm, "end": v(-14.5, 27.5) * mm});
            skArc(sketch, "E58.0.1.123", {"start": v(-88.5, 42.5) * mm, "mid": v(-90.62, 41.62) * mm, "end": v(-91.5, 39.5) * mm});
            skArc(sketch, "E58.0.1.124", {"start": v(-70.5, 24.5) * mm, "mid": v(-68.38, 25.38) * mm, "end": v(-67.5, 27.5) * mm});
            skArc(sketch, "E58.0.1.125", {"start": v(-35.5, 42.5) * mm, "mid": v(-37.62, 41.62) * mm, "end": v(-38.5, 39.5) * mm});
            skArc(sketch, "E58.0.1.126", {"start": v(9, 24.5) * mm, "mid": v(11.12, 25.38) * mm, "end": v(12, 27.5) * mm});
            skArc(sketch, "E58.0.1.127", {"start": v(70.5, 42.5) * mm, "mid": v(68.38, 41.62) * mm, "end": v(67.5, 39.5) * mm});
            skArc(sketch, "E58.0.1.128", {"start": v(123.5, 42.5) * mm, "mid": v(121.38, 41.62) * mm, "end": v(120.5, 39.5) * mm});
            skArc(sketch, "E58.0.1.129", {"start": v(17.5, 42.5) * mm, "mid": v(15.38, 41.62) * mm, "end": v(14.5, 39.5) * mm});
            skArc(sketch, "E58.0.1.130", {"start": v(-12, 27.5) * mm, "mid": v(-11.12, 25.38) * mm, "end": v(-9, 24.5) * mm});
            skArc(sketch, "E58.0.1.131", {"start": v(91.5, 39.5) * mm, "mid": v(90.62, 41.62) * mm, "end": v(88.5, 42.5) * mm});
            skArc(sketch, "E58.0.1.132", {"start": v(144.5, 39.5) * mm, "mid": v(143.62, 41.62) * mm, "end": v(141.5, 42.5) * mm});
            skArc(sketch, "E58.0.1.133", {"start": v(-41, 39.5) * mm, "mid": v(-41.88, 41.62) * mm, "end": v(-44, 42.5) * mm});
            skArc(sketch, "E58.0.1.134", {"start": v(88.5, 24.5) * mm, "mid": v(90.62, 25.38) * mm, "end": v(91.5, 27.5) * mm});
            skArc(sketch, "E58.0.1.135", {"start": v(141.5, 24.5) * mm, "mid": v(143.62, 25.38) * mm, "end": v(144.5, 27.5) * mm});
            skArc(sketch, "E58.0.1.136", {"start": v(-97, 24.5) * mm, "mid": v(-94.88, 25.38) * mm, "end": v(-94, 27.5) * mm});
            skArc(sketch, "E58.0.1.137", {"start": v(35.5, 24.5) * mm, "mid": v(37.62, 25.38) * mm, "end": v(38.5, 27.5) * mm});
            skArc(sketch, "E58.0.1.138", {"start": v(-44, 24.5) * mm, "mid": v(-41.88, 25.38) * mm, "end": v(-41, 27.5) * mm});
            skArc(sketch, "E58.0.1.139", {"start": v(-14.5, 39.5) * mm, "mid": v(-15.38, 41.62) * mm, "end": v(-17.5, 42.5) * mm});
            skArc(sketch, "E58.0.1.140", {"start": v(-120.5, 39.5) * mm, "mid": v(-121.38, 41.62) * mm, "end": v(-123.5, 42.5) * mm});
            skArc(sketch, "E58.0.1.141", {"start": v(-67.5, 39.5) * mm, "mid": v(-68.38, 41.62) * mm, "end": v(-70.5, 42.5) * mm});
            skArc(sketch, "E58.0.1.142", {"start": v(-144.5, 27.5) * mm, "mid": v(-143.62, 25.38) * mm, "end": v(-141.5, 24.5) * mm});
            skArc(sketch, "E58.0.1.143", {"start": v(-141.5, 42.5) * mm, "mid": v(-143.62, 41.62) * mm, "end": v(-144.5, 39.5) * mm});
            skArc(sketch, "E58.0.1.144", {"start": v(97, 42.5) * mm, "mid": v(94.88, 41.62) * mm, "end": v(94, 39.5) * mm});
            skArc(sketch, "E58.0.1.145", {"start": v(-123.5, 24.5) * mm, "mid": v(-121.38, 25.38) * mm, "end": v(-120.5, 27.5) * mm});
            skPoint(sketch, "E58.0.2.0", {"position": v(41, 63) * mm});
            skPoint(sketch, "E58.0.2.1", {"position": v(106, 54) * mm});
            skPoint(sketch, "E58.0.2.2", {"position": v(-38.5, 63) * mm});
            skLineSegment(sketch, "E58.0.2.3", {"start": v(-9, 63) * mm, "end": v(9, 63) * mm});
            skPoint(sketch, "E58.0.2.5", {"position": v(-94, 63) * mm});
            skPoint(sketch, "E58.0.2.6", {"position": v(65, 63) * mm});
            skPoint(sketch, "E58.0.2.7", {"position": v(118, 45) * mm});
            skPoint(sketch, "E58.0.2.8", {"position": v(12, 45) * mm});
            skPoint(sketch, "E58.0.2.9", {"position": v(-94, 45) * mm});
            skPoint(sketch, "E58.0.2.10", {"position": v(53, 54) * mm});
            skPoint(sketch, "E58.0.2.11", {"position": v(94, 45) * mm});
            skPoint(sketch, "E58.0.2.12", {"position": v(65, 45) * mm});
            skPoint(sketch, "E58.0.2.13", {"position": v(-118, 45) * mm});
            skPoint(sketch, "E58.0.2.14", {"position": v(-41, 63) * mm});
            skPoint(sketch, "E58.0.2.15", {"position": v(12, 63) * mm});
            skLineSegment(sketch, "E58.0.2.16", {"start": v(-62, 63) * mm, "end": v(-44, 63) * mm});
            skLineSegment(sketch, "E58.0.2.17", {"start": v(-115, 63) * mm, "end": v(-97, 63) * mm});
            skPoint(sketch, "E58.0.2.18", {"position": v(-106, 54) * mm});
            skPoint(sketch, "E58.0.2.19", {"position": v(41, 45) * mm});
            skPoint(sketch, "E58.0.2.20", {"position": v(-41, 45) * mm});
            skLineSegment(sketch, "E58.0.2.21", {"start": v(17.5, 45) * mm, "end": v(35.5, 45) * mm});
            skPoint(sketch, "E58.0.2.22", {"position": v(-118, 63) * mm});
            skPoint(sketch, "E58.0.2.23", {"position": v(120.5, 63) * mm});
            skPoint(sketch, "E58.0.2.24", {"position": v(-65, 45) * mm});
            skPoint(sketch, "E58.0.2.25", {"position": v(-12, 63) * mm});
            skPoint(sketch, "E58.0.2.26", {"position": v(67.5, 45) * mm});
            skPoint(sketch, "E58.0.2.27", {"position": v(26.5, 54) * mm});
            skPoint(sketch, "E58.0.2.28", {"position": v(118, 63) * mm});
            skPoint(sketch, "E58.0.2.29", {"position": v(-12, 45) * mm});
            skPoint(sketch, "E58.0.2.30", {"position": v(-26.5, 54) * mm});
            skPoint(sketch, "E58.0.2.31", {"position": v(94, 63) * mm});
            skPoint(sketch, "E58.0.2.32", {"position": v(-91.5, 63) * mm});
            skPoint(sketch, "E58.0.2.33", {"position": v(-38.5, 45) * mm});
            skLineSegment(sketch, "E58.0.2.34", {"start": v(44, 63) * mm, "end": v(62, 63) * mm});
            skLineSegment(sketch, "E58.0.2.35", {"start": v(97, 63) * mm, "end": v(115, 63) * mm});
            skPoint(sketch, "E58.0.2.36", {"position": v(144.5, 45) * mm});
            skPoint(sketch, "E58.0.2.37", {"position": v(91.5, 63) * mm});
            skPoint(sketch, "E58.0.2.38", {"position": v(14.5, 45) * mm});
            skPoint(sketch, "E58.0.2.39", {"position": v(-79.5, 54) * mm});
            skPoint(sketch, "E58.0.2.40", {"position": v(-14.5, 45) * mm});
            skLineSegment(sketch, "E58.0.2.41", {"start": v(97, 45) * mm, "end": v(115, 45) * mm});
            skPoint(sketch, "E58.0.2.42", {"position": v(-120.5, 63) * mm});
            skLineSegment(sketch, "E58.0.2.43", {"start": v(-141.5, 45) * mm, "end": v(-123.5, 45) * mm});
            skLineSegment(sketch, "E58.0.2.44", {"start": v(44, 45) * mm, "end": v(62, 45) * mm});
            skLineSegment(sketch, "E58.0.2.45", {"start": v(-88.5, 45) * mm, "end": v(-70.5, 45) * mm});
            skPoint(sketch, "E58.0.2.46", {"position": v(91.5, 45) * mm});
            skPoint(sketch, "E58.0.2.47", {"position": v(38.5, 63) * mm});
            skPoint(sketch, "E58.0.2.48", {"position": v(-67.5, 63) * mm});
            skPoint(sketch, "E58.0.2.49", {"position": v(-144.5, 45) * mm});
            skPoint(sketch, "E58.0.2.50", {"position": v(38.5, 45) * mm});
            skPoint(sketch, "E58.0.2.51", {"position": v(-91.5, 45) * mm});
            skPoint(sketch, "E58.0.2.52", {"position": v(-144.5, 63) * mm});
            skPoint(sketch, "E58.0.2.53", {"position": v(-14.5, 63) * mm});
            skLineSegment(sketch, "E58.0.2.54", {"start": v(-35.5, 63) * mm, "end": v(-17.5, 63) * mm});
            skLineSegment(sketch, "E58.0.2.55", {"start": v(-141.5, 63) * mm, "end": v(-123.5, 63) * mm});
            skPoint(sketch, "E58.0.2.56", {"position": v(-65, 63) * mm});
            skLineSegment(sketch, "E58.0.2.57", {"start": v(-88.5, 63) * mm, "end": v(-70.5, 63) * mm});
            skPoint(sketch, "E58.0.2.58", {"position": v(67.5, 63) * mm});
            skPoint(sketch, "E58.0.2.59", {"position": v(132.5, 54) * mm});
            skLineSegment(sketch, "E58.0.2.60", {"start": v(-12, 45) * mm, "end": v(-38.5, 45) * mm, "construction": true});
            skLineSegment(sketch, "E58.0.2.61", {"start": v(17.5, 63) * mm, "end": v(35.5, 63) * mm});
            skPoint(sketch, "E58.0.2.62", {"position": v(79.5, 54) * mm});
            skPoint(sketch, "E58.0.2.63", {"position": v(14.5, 63) * mm});
            skPoint(sketch, "E58.0.2.64", {"position": v(-120.5, 45) * mm});
            skPoint(sketch, "E58.0.2.65", {"position": v(-132.5, 54) * mm});
            skPoint(sketch, "E58.0.2.66", {"position": v(-67.5, 45) * mm});
            skPoint(sketch, "E58.0.2.67", {"position": v(0, 54) * mm});
            skPoint(sketch, "E58.0.2.68", {"position": v(120.5, 45) * mm});
            skLineSegment(sketch, "E58.0.2.69", {"start": v(70.5, 63) * mm, "end": v(88.5, 63) * mm});
            skLineSegment(sketch, "E58.0.2.70", {"start": v(123.5, 63) * mm, "end": v(141.5, 63) * mm});
            skLineSegment(sketch, "E58.0.2.71", {"start": v(70.5, 45) * mm, "end": v(88.5, 45) * mm});
            skLineSegment(sketch, "E58.0.2.72", {"start": v(123.5, 45) * mm, "end": v(141.5, 45) * mm});
            skLineSegment(sketch, "E58.0.2.73", {"start": v(-115, 45) * mm, "end": v(-97, 45) * mm});
            skPoint(sketch, "E58.0.2.74", {"position": v(-53, 54) * mm});
            skPoint(sketch, "E58.0.2.75", {"position": v(144.5, 63) * mm});
            skLineSegment(sketch, "E58.0.2.76", {"start": v(-62, 45) * mm, "end": v(-44, 45) * mm});
            skLineSegment(sketch, "E58.0.2.77", {"start": v(118, 60) * mm, "end": v(118, 48) * mm});
            skLineSegment(sketch, "E58.0.2.78", {"start": v(-12, 45) * mm, "end": v(14.5, 45) * mm, "construction": true});
            skLineSegment(sketch, "E58.0.2.79", {"start": v(65, 60) * mm, "end": v(65, 48) * mm});
            skLineSegment(sketch, "E58.0.2.80", {"start": v(12, 60) * mm, "end": v(12, 48) * mm});
            skLineSegment(sketch, "E58.0.2.81", {"start": v(-12, 60) * mm, "end": v(-12, 48) * mm});
            skLineSegment(sketch, "E58.0.2.82", {"start": v(14.5, 60) * mm, "end": v(14.5, 48) * mm});
            skLineSegment(sketch, "E58.0.2.83", {"start": v(38.5, 60) * mm, "end": v(38.5, 48) * mm});
            skLineSegment(sketch, "E58.0.2.84", {"start": v(-14.5, 60) * mm, "end": v(-14.5, 48) * mm});
            skLineSegment(sketch, "E58.0.2.85", {"start": v(94, 60) * mm, "end": v(94, 48) * mm});
            skLineSegment(sketch, "E58.0.2.86", {"start": v(41, 60) * mm, "end": v(41, 48) * mm});
            skLineSegment(sketch, "E58.0.2.87", {"start": v(-120.5, 60) * mm, "end": v(-120.5, 48) * mm});
            skLineSegment(sketch, "E58.0.2.88", {"start": v(-67.5, 60) * mm, "end": v(-67.5, 48) * mm});
            skLineSegment(sketch, "E58.0.2.89", {"start": v(-38.5, 60) * mm, "end": v(-38.5, 48) * mm});
            skLineSegment(sketch, "E58.0.2.90", {"start": v(-144.5, 60) * mm, "end": v(-144.5, 48) * mm});
            skLineSegment(sketch, "E58.0.2.91", {"start": v(-91.5, 60) * mm, "end": v(-91.5, 48) * mm});
            skLineSegment(sketch, "E58.0.2.92", {"start": v(-35.5, 45) * mm, "end": v(-17.5, 45) * mm});
            skLineSegment(sketch, "E58.0.2.93", {"start": v(144.5, 60) * mm, "end": v(144.5, 48) * mm});
            skLineSegment(sketch, "E58.0.2.94", {"start": v(91.5, 60) * mm, "end": v(91.5, 48) * mm});
            skLineSegment(sketch, "E58.0.2.95", {"start": v(-94, 60) * mm, "end": v(-94, 48) * mm});
            skLineSegment(sketch, "E58.0.2.96", {"start": v(-41, 60) * mm, "end": v(-41, 48) * mm});
            skLineSegment(sketch, "E58.0.2.97", {"start": v(120.5, 60) * mm, "end": v(120.5, 48) * mm});
            skLineSegment(sketch, "E58.0.2.98", {"start": v(67.5, 60) * mm, "end": v(67.5, 48) * mm});
            skLineSegment(sketch, "E58.0.2.99", {"start": v(-118, 60) * mm, "end": v(-118, 48) * mm});
            skLineSegment(sketch, "E58.0.2.100", {"start": v(-65, 60) * mm, "end": v(-65, 48) * mm});
            skArc(sketch, "E58.0.2.101", {"start": v(-65, 48) * mm, "mid": v(-64.12, 45.88) * mm, "end": v(-62, 45) * mm});
            skArc(sketch, "E58.0.2.102", {"start": v(-118, 48) * mm, "mid": v(-117.12, 45.88) * mm, "end": v(-115, 45) * mm});
            skArc(sketch, "E58.0.2.103", {"start": v(12, 60) * mm, "mid": v(11.12, 62.12) * mm, "end": v(9, 63) * mm});
            skArc(sketch, "E58.0.2.104", {"start": v(-9, 63) * mm, "mid": v(-11.12, 62.12) * mm, "end": v(-12, 60) * mm});
            skLineSegment(sketch, "E58.0.2.105", {"start": v(-9, 45) * mm, "end": v(9, 45) * mm});
            skArc(sketch, "E58.0.2.106", {"start": v(-62, 63) * mm, "mid": v(-64.12, 62.12) * mm, "end": v(-65, 60) * mm});
            skArc(sketch, "E58.0.2.107", {"start": v(-115, 63) * mm, "mid": v(-117.12, 62.12) * mm, "end": v(-118, 60) * mm});
            skArc(sketch, "E58.0.2.108", {"start": v(-94, 60) * mm, "mid": v(-94.88, 62.12) * mm, "end": v(-97, 63) * mm});
            skArc(sketch, "E58.0.2.109", {"start": v(38.5, 60) * mm, "mid": v(37.62, 62.12) * mm, "end": v(35.5, 63) * mm});
            skArc(sketch, "E58.0.2.110", {"start": v(67.5, 48) * mm, "mid": v(68.38, 45.88) * mm, "end": v(70.5, 45) * mm});
            skArc(sketch, "E58.0.2.111", {"start": v(120.5, 48) * mm, "mid": v(121.38, 45.88) * mm, "end": v(123.5, 45) * mm});
            skArc(sketch, "E58.0.2.112", {"start": v(14.5, 48) * mm, "mid": v(15.38, 45.88) * mm, "end": v(17.5, 45) * mm});
            skArc(sketch, "E58.0.2.113", {"start": v(65, 60) * mm, "mid": v(64.12, 62.12) * mm, "end": v(62, 63) * mm});
            skArc(sketch, "E58.0.2.114", {"start": v(118, 60) * mm, "mid": v(117.12, 62.12) * mm, "end": v(115, 63) * mm});
            skArc(sketch, "E58.0.2.115", {"start": v(-91.5, 48) * mm, "mid": v(-90.62, 45.88) * mm, "end": v(-88.5, 45) * mm});
            skArc(sketch, "E58.0.2.116", {"start": v(-38.5, 48) * mm, "mid": v(-37.62, 45.88) * mm, "end": v(-35.5, 45) * mm});
            skArc(sketch, "E58.0.2.117", {"start": v(94, 48) * mm, "mid": v(94.88, 45.88) * mm, "end": v(97, 45) * mm});
            skArc(sketch, "E58.0.2.118", {"start": v(41, 48) * mm, "mid": v(41.88, 45.88) * mm, "end": v(44, 45) * mm});
            skArc(sketch, "E58.0.2.119", {"start": v(115, 45) * mm, "mid": v(117.12, 45.88) * mm, "end": v(118, 48) * mm});
            skArc(sketch, "E58.0.2.120", {"start": v(62, 45) * mm, "mid": v(64.12, 45.88) * mm, "end": v(65, 48) * mm});
            skArc(sketch, "E58.0.2.121", {"start": v(44, 63) * mm, "mid": v(41.88, 62.12) * mm, "end": v(41, 60) * mm});
            skArc(sketch, "E58.0.2.122", {"start": v(-17.5, 45) * mm, "mid": v(-15.38, 45.88) * mm, "end": v(-14.5, 48) * mm});
            skArc(sketch, "E58.0.2.123", {"start": v(-88.5, 63) * mm, "mid": v(-90.62, 62.12) * mm, "end": v(-91.5, 60) * mm});
            skArc(sketch, "E58.0.2.124", {"start": v(-70.5, 45) * mm, "mid": v(-68.38, 45.88) * mm, "end": v(-67.5, 48) * mm});
            skArc(sketch, "E58.0.2.125", {"start": v(-35.5, 63) * mm, "mid": v(-37.62, 62.12) * mm, "end": v(-38.5, 60) * mm});
            skArc(sketch, "E58.0.2.126", {"start": v(9, 45) * mm, "mid": v(11.12, 45.88) * mm, "end": v(12, 48) * mm});
            skArc(sketch, "E58.0.2.127", {"start": v(70.5, 63) * mm, "mid": v(68.38, 62.12) * mm, "end": v(67.5, 60) * mm});
            skArc(sketch, "E58.0.2.128", {"start": v(123.5, 63) * mm, "mid": v(121.38, 62.12) * mm, "end": v(120.5, 60) * mm});
            skArc(sketch, "E58.0.2.129", {"start": v(17.5, 63) * mm, "mid": v(15.38, 62.12) * mm, "end": v(14.5, 60) * mm});
            skArc(sketch, "E58.0.2.130", {"start": v(-12, 48) * mm, "mid": v(-11.12, 45.88) * mm, "end": v(-9, 45) * mm});
            skArc(sketch, "E58.0.2.131", {"start": v(91.5, 60) * mm, "mid": v(90.62, 62.12) * mm, "end": v(88.5, 63) * mm});
            skArc(sketch, "E58.0.2.132", {"start": v(144.5, 60) * mm, "mid": v(143.62, 62.12) * mm, "end": v(141.5, 63) * mm});
            skArc(sketch, "E58.0.2.133", {"start": v(-41, 60) * mm, "mid": v(-41.88, 62.12) * mm, "end": v(-44, 63) * mm});
            skArc(sketch, "E58.0.2.134", {"start": v(88.5, 45) * mm, "mid": v(90.62, 45.88) * mm, "end": v(91.5, 48) * mm});
            skArc(sketch, "E58.0.2.135", {"start": v(141.5, 45) * mm, "mid": v(143.62, 45.88) * mm, "end": v(144.5, 48) * mm});
            skArc(sketch, "E58.0.2.136", {"start": v(-97, 45) * mm, "mid": v(-94.88, 45.88) * mm, "end": v(-94, 48) * mm});
            skArc(sketch, "E58.0.2.137", {"start": v(35.5, 45) * mm, "mid": v(37.62, 45.88) * mm, "end": v(38.5, 48) * mm});
            skArc(sketch, "E58.0.2.138", {"start": v(-44, 45) * mm, "mid": v(-41.88, 45.88) * mm, "end": v(-41, 48) * mm});
            skArc(sketch, "E58.0.2.139", {"start": v(-14.5, 60) * mm, "mid": v(-15.38, 62.12) * mm, "end": v(-17.5, 63) * mm});
            skArc(sketch, "E58.0.2.140", {"start": v(-120.5, 60) * mm, "mid": v(-121.38, 62.12) * mm, "end": v(-123.5, 63) * mm});
            skArc(sketch, "E58.0.2.141", {"start": v(-67.5, 60) * mm, "mid": v(-68.38, 62.12) * mm, "end": v(-70.5, 63) * mm});
            skArc(sketch, "E58.0.2.142", {"start": v(-144.5, 48) * mm, "mid": v(-143.62, 45.88) * mm, "end": v(-141.5, 45) * mm});
            skArc(sketch, "E58.0.2.143", {"start": v(-141.5, 63) * mm, "mid": v(-143.62, 62.12) * mm, "end": v(-144.5, 60) * mm});
            skArc(sketch, "E58.0.2.144", {"start": v(97, 63) * mm, "mid": v(94.88, 62.12) * mm, "end": v(94, 60) * mm});
            skArc(sketch, "E58.0.2.145", {"start": v(-123.5, 45) * mm, "mid": v(-121.38, 45.88) * mm, "end": v(-120.5, 48) * mm});
            skPoint(sketch, "E58.0.3.0", {"position": v(41, 83.5) * mm});
            skPoint(sketch, "E58.0.3.1", {"position": v(106, 74.5) * mm});
            skPoint(sketch, "E58.0.3.2", {"position": v(-38.5, 83.5) * mm});
            skLineSegment(sketch, "E58.0.3.3", {"start": v(-9, 83.5) * mm, "end": v(9, 83.5) * mm});
            skPoint(sketch, "E58.0.3.5", {"position": v(-94, 83.5) * mm});
            skPoint(sketch, "E58.0.3.6", {"position": v(65, 83.5) * mm});
            skPoint(sketch, "E58.0.3.7", {"position": v(118, 65.5) * mm});
            skPoint(sketch, "E58.0.3.8", {"position": v(12, 65.5) * mm});
            skPoint(sketch, "E58.0.3.9", {"position": v(-94, 65.5) * mm});
            skPoint(sketch, "E58.0.3.10", {"position": v(53, 74.5) * mm});
            skPoint(sketch, "E58.0.3.11", {"position": v(94, 65.5) * mm});
            skPoint(sketch, "E58.0.3.12", {"position": v(65, 65.5) * mm});
            skPoint(sketch, "E58.0.3.13", {"position": v(-118, 65.5) * mm});
            skPoint(sketch, "E58.0.3.14", {"position": v(-41, 83.5) * mm});
            skPoint(sketch, "E58.0.3.15", {"position": v(12, 83.5) * mm});
            skLineSegment(sketch, "E58.0.3.16", {"start": v(-62, 83.5) * mm, "end": v(-44, 83.5) * mm});
            skLineSegment(sketch, "E58.0.3.17", {"start": v(-115, 83.5) * mm, "end": v(-97, 83.5) * mm});
            skPoint(sketch, "E58.0.3.18", {"position": v(-106, 74.5) * mm});
            skPoint(sketch, "E58.0.3.19", {"position": v(41, 65.5) * mm});
            skPoint(sketch, "E58.0.3.20", {"position": v(-41, 65.5) * mm});
            skLineSegment(sketch, "E58.0.3.21", {"start": v(17.5, 65.5) * mm, "end": v(35.5, 65.5) * mm});
            skPoint(sketch, "E58.0.3.22", {"position": v(-118, 83.5) * mm});
            skPoint(sketch, "E58.0.3.23", {"position": v(120.5, 83.5) * mm});
            skPoint(sketch, "E58.0.3.24", {"position": v(-65, 65.5) * mm});
            skPoint(sketch, "E58.0.3.25", {"position": v(-12, 83.5) * mm});
            skPoint(sketch, "E58.0.3.26", {"position": v(67.5, 65.5) * mm});
            skPoint(sketch, "E58.0.3.27", {"position": v(26.5, 74.5) * mm});
            skPoint(sketch, "E58.0.3.28", {"position": v(118, 83.5) * mm});
            skPoint(sketch, "E58.0.3.29", {"position": v(-12, 65.5) * mm});
            skPoint(sketch, "E58.0.3.30", {"position": v(-26.5, 74.5) * mm});
            skPoint(sketch, "E58.0.3.31", {"position": v(94, 83.5) * mm});
            skPoint(sketch, "E58.0.3.32", {"position": v(-91.5, 83.5) * mm});
            skPoint(sketch, "E58.0.3.33", {"position": v(-38.5, 65.5) * mm});
            skLineSegment(sketch, "E58.0.3.34", {"start": v(44, 83.5) * mm, "end": v(62, 83.5) * mm});
            skLineSegment(sketch, "E58.0.3.35", {"start": v(97, 83.5) * mm, "end": v(115, 83.5) * mm});
            skPoint(sketch, "E58.0.3.36", {"position": v(144.5, 65.5) * mm});
            skPoint(sketch, "E58.0.3.37", {"position": v(91.5, 83.5) * mm});
            skPoint(sketch, "E58.0.3.38", {"position": v(14.5, 65.5) * mm});
            skPoint(sketch, "E58.0.3.39", {"position": v(-79.5, 74.5) * mm});
            skPoint(sketch, "E58.0.3.40", {"position": v(-14.5, 65.5) * mm});
            skLineSegment(sketch, "E58.0.3.41", {"start": v(97, 65.5) * mm, "end": v(115, 65.5) * mm});
            skPoint(sketch, "E58.0.3.42", {"position": v(-120.5, 83.5) * mm});
            skLineSegment(sketch, "E58.0.3.43", {"start": v(-141.5, 65.5) * mm, "end": v(-123.5, 65.5) * mm});
            skLineSegment(sketch, "E58.0.3.44", {"start": v(44, 65.5) * mm, "end": v(62, 65.5) * mm});
            skLineSegment(sketch, "E58.0.3.45", {"start": v(-88.5, 65.5) * mm, "end": v(-70.5, 65.5) * mm});
            skPoint(sketch, "E58.0.3.46", {"position": v(91.5, 65.5) * mm});
            skPoint(sketch, "E58.0.3.47", {"position": v(38.5, 83.5) * mm});
            skPoint(sketch, "E58.0.3.48", {"position": v(-67.5, 83.5) * mm});
            skPoint(sketch, "E58.0.3.49", {"position": v(-144.5, 65.5) * mm});
            skPoint(sketch, "E58.0.3.50", {"position": v(38.5, 65.5) * mm});
            skPoint(sketch, "E58.0.3.51", {"position": v(-91.5, 65.5) * mm});
            skPoint(sketch, "E58.0.3.52", {"position": v(-144.5, 83.5) * mm});
            skPoint(sketch, "E58.0.3.53", {"position": v(-14.5, 83.5) * mm});
            skLineSegment(sketch, "E58.0.3.54", {"start": v(-35.5, 83.5) * mm, "end": v(-17.5, 83.5) * mm});
            skLineSegment(sketch, "E58.0.3.55", {"start": v(-141.5, 83.5) * mm, "end": v(-123.5, 83.5) * mm});
            skPoint(sketch, "E58.0.3.56", {"position": v(-65, 83.5) * mm});
            skLineSegment(sketch, "E58.0.3.57", {"start": v(-88.5, 83.5) * mm, "end": v(-70.5, 83.5) * mm});
            skPoint(sketch, "E58.0.3.58", {"position": v(67.5, 83.5) * mm});
            skPoint(sketch, "E58.0.3.59", {"position": v(132.5, 74.5) * mm});
            skLineSegment(sketch, "E58.0.3.60", {"start": v(-12, 65.5) * mm, "end": v(-38.5, 65.5) * mm, "construction": true});
            skLineSegment(sketch, "E58.0.3.61", {"start": v(17.5, 83.5) * mm, "end": v(35.5, 83.5) * mm});
            skPoint(sketch, "E58.0.3.62", {"position": v(79.5, 74.5) * mm});
            skPoint(sketch, "E58.0.3.63", {"position": v(14.5, 83.5) * mm});
            skPoint(sketch, "E58.0.3.64", {"position": v(-120.5, 65.5) * mm});
            skPoint(sketch, "E58.0.3.65", {"position": v(-132.5, 74.5) * mm});
            skPoint(sketch, "E58.0.3.66", {"position": v(-67.5, 65.5) * mm});
            skPoint(sketch, "E58.0.3.67", {"position": v(0, 74.5) * mm});
            skPoint(sketch, "E58.0.3.68", {"position": v(120.5, 65.5) * mm});
            skLineSegment(sketch, "E58.0.3.69", {"start": v(70.5, 83.5) * mm, "end": v(88.5, 83.5) * mm});
            skLineSegment(sketch, "E58.0.3.70", {"start": v(123.5, 83.5) * mm, "end": v(141.5, 83.5) * mm});
            skLineSegment(sketch, "E58.0.3.71", {"start": v(70.5, 65.5) * mm, "end": v(88.5, 65.5) * mm});
            skLineSegment(sketch, "E58.0.3.72", {"start": v(123.5, 65.5) * mm, "end": v(141.5, 65.5) * mm});
            skLineSegment(sketch, "E58.0.3.73", {"start": v(-115, 65.5) * mm, "end": v(-97, 65.5) * mm});
            skPoint(sketch, "E58.0.3.74", {"position": v(-53, 74.5) * mm});
            skPoint(sketch, "E58.0.3.75", {"position": v(144.5, 83.5) * mm});
            skLineSegment(sketch, "E58.0.3.76", {"start": v(-62, 65.5) * mm, "end": v(-44, 65.5) * mm});
            skLineSegment(sketch, "E58.0.3.77", {"start": v(118, 80.5) * mm, "end": v(118, 68.5) * mm});
            skLineSegment(sketch, "E58.0.3.78", {"start": v(-12, 65.5) * mm, "end": v(14.5, 65.5) * mm, "construction": true});
            skLineSegment(sketch, "E58.0.3.79", {"start": v(65, 80.5) * mm, "end": v(65, 68.5) * mm});
            skLineSegment(sketch, "E58.0.3.80", {"start": v(12, 80.5) * mm, "end": v(12, 68.5) * mm});
            skLineSegment(sketch, "E58.0.3.81", {"start": v(-12, 80.5) * mm, "end": v(-12, 68.5) * mm});
            skLineSegment(sketch, "E58.0.3.82", {"start": v(14.5, 80.5) * mm, "end": v(14.5, 68.5) * mm});
            skLineSegment(sketch, "E58.0.3.83", {"start": v(38.5, 80.5) * mm, "end": v(38.5, 68.5) * mm});
            skLineSegment(sketch, "E58.0.3.84", {"start": v(-14.5, 80.5) * mm, "end": v(-14.5, 68.5) * mm});
            skLineSegment(sketch, "E58.0.3.85", {"start": v(94, 80.5) * mm, "end": v(94, 68.5) * mm});
            skLineSegment(sketch, "E58.0.3.86", {"start": v(41, 80.5) * mm, "end": v(41, 68.5) * mm});
            skLineSegment(sketch, "E58.0.3.87", {"start": v(-120.5, 80.5) * mm, "end": v(-120.5, 68.5) * mm});
            skLineSegment(sketch, "E58.0.3.88", {"start": v(-67.5, 80.5) * mm, "end": v(-67.5, 68.5) * mm});
            skLineSegment(sketch, "E58.0.3.89", {"start": v(-38.5, 80.5) * mm, "end": v(-38.5, 68.5) * mm});
            skLineSegment(sketch, "E58.0.3.90", {"start": v(-144.5, 80.5) * mm, "end": v(-144.5, 68.5) * mm});
            skLineSegment(sketch, "E58.0.3.91", {"start": v(-91.5, 80.5) * mm, "end": v(-91.5, 68.5) * mm});
            skLineSegment(sketch, "E58.0.3.92", {"start": v(-35.5, 65.5) * mm, "end": v(-17.5, 65.5) * mm});
            skLineSegment(sketch, "E58.0.3.93", {"start": v(144.5, 80.5) * mm, "end": v(144.5, 68.5) * mm});
            skLineSegment(sketch, "E58.0.3.94", {"start": v(91.5, 80.5) * mm, "end": v(91.5, 68.5) * mm});
            skLineSegment(sketch, "E58.0.3.95", {"start": v(-94, 80.5) * mm, "end": v(-94, 68.5) * mm});
            skLineSegment(sketch, "E58.0.3.96", {"start": v(-41, 80.5) * mm, "end": v(-41, 68.5) * mm});
            skLineSegment(sketch, "E58.0.3.97", {"start": v(120.5, 80.5) * mm, "end": v(120.5, 68.5) * mm});
            skLineSegment(sketch, "E58.0.3.98", {"start": v(67.5, 80.5) * mm, "end": v(67.5, 68.5) * mm});
            skLineSegment(sketch, "E58.0.3.99", {"start": v(-118, 80.5) * mm, "end": v(-118, 68.5) * mm});
            skLineSegment(sketch, "E58.0.3.100", {"start": v(-65, 80.5) * mm, "end": v(-65, 68.5) * mm});
            skArc(sketch, "E58.0.3.101", {"start": v(-65, 68.5) * mm, "mid": v(-64.12, 66.38) * mm, "end": v(-62, 65.5) * mm});
            skArc(sketch, "E58.0.3.102", {"start": v(-118, 68.5) * mm, "mid": v(-117.12, 66.38) * mm, "end": v(-115, 65.5) * mm});
            skArc(sketch, "E58.0.3.103", {"start": v(12, 80.5) * mm, "mid": v(11.12, 82.62) * mm, "end": v(9, 83.5) * mm});
            skArc(sketch, "E58.0.3.104", {"start": v(-9, 83.5) * mm, "mid": v(-11.12, 82.62) * mm, "end": v(-12, 80.5) * mm});
            skLineSegment(sketch, "E58.0.3.105", {"start": v(-9, 65.5) * mm, "end": v(9, 65.5) * mm});
            skArc(sketch, "E58.0.3.106", {"start": v(-62, 83.5) * mm, "mid": v(-64.12, 82.62) * mm, "end": v(-65, 80.5) * mm});
            skArc(sketch, "E58.0.3.107", {"start": v(-115, 83.5) * mm, "mid": v(-117.12, 82.62) * mm, "end": v(-118, 80.5) * mm});
            skArc(sketch, "E58.0.3.108", {"start": v(-94, 80.5) * mm, "mid": v(-94.88, 82.62) * mm, "end": v(-97, 83.5) * mm});
            skArc(sketch, "E58.0.3.109", {"start": v(38.5, 80.5) * mm, "mid": v(37.62, 82.62) * mm, "end": v(35.5, 83.5) * mm});
            skArc(sketch, "E58.0.3.110", {"start": v(67.5, 68.5) * mm, "mid": v(68.38, 66.38) * mm, "end": v(70.5, 65.5) * mm});
            skArc(sketch, "E58.0.3.111", {"start": v(120.5, 68.5) * mm, "mid": v(121.38, 66.38) * mm, "end": v(123.5, 65.5) * mm});
            skArc(sketch, "E58.0.3.112", {"start": v(14.5, 68.5) * mm, "mid": v(15.38, 66.38) * mm, "end": v(17.5, 65.5) * mm});
            skArc(sketch, "E58.0.3.113", {"start": v(65, 80.5) * mm, "mid": v(64.12, 82.62) * mm, "end": v(62, 83.5) * mm});
            skArc(sketch, "E58.0.3.114", {"start": v(118, 80.5) * mm, "mid": v(117.12, 82.62) * mm, "end": v(115, 83.5) * mm});
            skArc(sketch, "E58.0.3.115", {"start": v(-91.5, 68.5) * mm, "mid": v(-90.62, 66.38) * mm, "end": v(-88.5, 65.5) * mm});
            skArc(sketch, "E58.0.3.116", {"start": v(-38.5, 68.5) * mm, "mid": v(-37.62, 66.38) * mm, "end": v(-35.5, 65.5) * mm});
            skArc(sketch, "E58.0.3.117", {"start": v(94, 68.5) * mm, "mid": v(94.88, 66.38) * mm, "end": v(97, 65.5) * mm});
            skArc(sketch, "E58.0.3.118", {"start": v(41, 68.5) * mm, "mid": v(41.88, 66.38) * mm, "end": v(44, 65.5) * mm});
            skArc(sketch, "E58.0.3.119", {"start": v(115, 65.5) * mm, "mid": v(117.12, 66.38) * mm, "end": v(118, 68.5) * mm});
            skArc(sketch, "E58.0.3.120", {"start": v(62, 65.5) * mm, "mid": v(64.12, 66.38) * mm, "end": v(65, 68.5) * mm});
            skArc(sketch, "E58.0.3.121", {"start": v(44, 83.5) * mm, "mid": v(41.88, 82.62) * mm, "end": v(41, 80.5) * mm});
            skArc(sketch, "E58.0.3.122", {"start": v(-17.5, 65.5) * mm, "mid": v(-15.38, 66.38) * mm, "end": v(-14.5, 68.5) * mm});
            skArc(sketch, "E58.0.3.123", {"start": v(-88.5, 83.5) * mm, "mid": v(-90.62, 82.62) * mm, "end": v(-91.5, 80.5) * mm});
            skArc(sketch, "E58.0.3.124", {"start": v(-70.5, 65.5) * mm, "mid": v(-68.38, 66.38) * mm, "end": v(-67.5, 68.5) * mm});
            skArc(sketch, "E58.0.3.125", {"start": v(-35.5, 83.5) * mm, "mid": v(-37.62, 82.62) * mm, "end": v(-38.5, 80.5) * mm});
            skArc(sketch, "E58.0.3.126", {"start": v(9, 65.5) * mm, "mid": v(11.12, 66.38) * mm, "end": v(12, 68.5) * mm});
            skArc(sketch, "E58.0.3.127", {"start": v(70.5, 83.5) * mm, "mid": v(68.38, 82.62) * mm, "end": v(67.5, 80.5) * mm});
            skArc(sketch, "E58.0.3.128", {"start": v(123.5, 83.5) * mm, "mid": v(121.38, 82.62) * mm, "end": v(120.5, 80.5) * mm});
            skArc(sketch, "E58.0.3.129", {"start": v(17.5, 83.5) * mm, "mid": v(15.38, 82.62) * mm, "end": v(14.5, 80.5) * mm});
            skArc(sketch, "E58.0.3.130", {"start": v(-12, 68.5) * mm, "mid": v(-11.12, 66.38) * mm, "end": v(-9, 65.5) * mm});
            skArc(sketch, "E58.0.3.131", {"start": v(91.5, 80.5) * mm, "mid": v(90.62, 82.62) * mm, "end": v(88.5, 83.5) * mm});
            skArc(sketch, "E58.0.3.132", {"start": v(144.5, 80.5) * mm, "mid": v(143.62, 82.62) * mm, "end": v(141.5, 83.5) * mm});
            skArc(sketch, "E58.0.3.133", {"start": v(-41, 80.5) * mm, "mid": v(-41.88, 82.62) * mm, "end": v(-44, 83.5) * mm});
            skArc(sketch, "E58.0.3.134", {"start": v(88.5, 65.5) * mm, "mid": v(90.62, 66.38) * mm, "end": v(91.5, 68.5) * mm});
            skArc(sketch, "E58.0.3.135", {"start": v(141.5, 65.5) * mm, "mid": v(143.62, 66.38) * mm, "end": v(144.5, 68.5) * mm});
            skArc(sketch, "E58.0.3.136", {"start": v(-97, 65.5) * mm, "mid": v(-94.88, 66.38) * mm, "end": v(-94, 68.5) * mm});
            skArc(sketch, "E58.0.3.137", {"start": v(35.5, 65.5) * mm, "mid": v(37.62, 66.38) * mm, "end": v(38.5, 68.5) * mm});
            skArc(sketch, "E58.0.3.138", {"start": v(-44, 65.5) * mm, "mid": v(-41.88, 66.38) * mm, "end": v(-41, 68.5) * mm});
            skArc(sketch, "E58.0.3.139", {"start": v(-14.5, 80.5) * mm, "mid": v(-15.38, 82.62) * mm, "end": v(-17.5, 83.5) * mm});
            skArc(sketch, "E58.0.3.140", {"start": v(-120.5, 80.5) * mm, "mid": v(-121.38, 82.62) * mm, "end": v(-123.5, 83.5) * mm});
            skArc(sketch, "E58.0.3.141", {"start": v(-67.5, 80.5) * mm, "mid": v(-68.38, 82.62) * mm, "end": v(-70.5, 83.5) * mm});
            skArc(sketch, "E58.0.3.142", {"start": v(-144.5, 68.5) * mm, "mid": v(-143.62, 66.38) * mm, "end": v(-141.5, 65.5) * mm});
            skArc(sketch, "E58.0.3.143", {"start": v(-141.5, 83.5) * mm, "mid": v(-143.62, 82.62) * mm, "end": v(-144.5, 80.5) * mm});
            skArc(sketch, "E58.0.3.144", {"start": v(97, 83.5) * mm, "mid": v(94.88, 82.62) * mm, "end": v(94, 80.5) * mm});
            skArc(sketch, "E58.0.3.145", {"start": v(-123.5, 65.5) * mm, "mid": v(-121.38, 66.38) * mm, "end": v(-120.5, 68.5) * mm});
            skLineSegment(sketch, "E58.direction1", {"start": v(-144.5, 4) * mm, "end": v(-119.5, 4) * mm, "construction": true});
            skLineSegment(sketch, "E58.direction2", {"start": v(-144.5, 4) * mm, "end": v(-144.5, 24.5) * mm, "construction": true});
            skPoint(sketch, "E59.0.1.0", {"position": v(118, -16.5) * mm});
            skPoint(sketch, "E59.0.1.1", {"position": v(94, -16.5) * mm});
            skLineSegment(sketch, "E59.0.1.2", {"start": v(-12, -1.5) * mm, "end": v(-12, -13.5) * mm});
            skLineSegment(sketch, "E59.0.1.3", {"start": v(12, -1.5) * mm, "end": v(12, -13.5) * mm});
            skLineSegment(sketch, "E59.0.1.5", {"start": v(-88.5, 1.5) * mm, "end": v(-70.5, 1.5) * mm});
            skLineSegment(sketch, "E59.0.1.6", {"start": v(-141.5, 1.5) * mm, "end": v(-123.5, 1.5) * mm});
            skLineSegment(sketch, "E59.0.1.7", {"start": v(-35.5, 1.5) * mm, "end": v(-17.5, 1.5) * mm});
            skPoint(sketch, "E59.0.1.8", {"position": v(-118, -16.5) * mm});
            skPoint(sketch, "E59.0.1.9", {"position": v(65, -16.5) * mm});
            skLineSegment(sketch, "E59.0.1.12", {"start": v(-88.5, -16.5) * mm, "end": v(-70.5, -16.5) * mm});
            skLineSegment(sketch, "E59.0.1.13", {"start": v(44, -16.5) * mm, "end": v(62, -16.5) * mm});
            skLineSegment(sketch, "E59.0.1.14", {"start": v(97, -16.5) * mm, "end": v(115, -16.5) * mm});
            skPoint(sketch, "E59.0.1.15", {"position": v(-41, -16.5) * mm});
            skPoint(sketch, "E59.0.1.16", {"position": v(-106, -7.5) * mm});
            skPoint(sketch, "E59.0.1.17", {"position": v(41, -16.5) * mm});
            skLineSegment(sketch, "E59.0.1.18", {"start": v(-91.5, -1.5) * mm, "end": v(-91.5, -13.5) * mm});
            skLineSegment(sketch, "E59.0.1.21", {"start": v(44, 1.5) * mm, "end": v(62, 1.5) * mm});
            skLineSegment(sketch, "E59.0.1.22", {"start": v(97, 1.5) * mm, "end": v(115, 1.5) * mm});
            skLineSegment(sketch, "E59.0.1.23", {"start": v(-38.5, -1.5) * mm, "end": v(-38.5, -13.5) * mm});
            skPoint(sketch, "E59.0.1.24", {"position": v(-65, -16.5) * mm});
            skLineSegment(sketch, "E59.0.1.25", {"start": v(-67.5, -1.5) * mm, "end": v(-67.5, -13.5) * mm});
            skLineSegment(sketch, "E59.0.1.26", {"start": v(41, -1.5) * mm, "end": v(41, -13.5) * mm});
            skLineSegment(sketch, "E59.0.1.27", {"start": v(94, -1.5) * mm, "end": v(94, -13.5) * mm});
            skLineSegment(sketch, "E59.0.1.28", {"start": v(-14.5, -1.5) * mm, "end": v(-14.5, -13.5) * mm});
            skPoint(sketch, "E59.0.1.29", {"position": v(-94, -16.5) * mm});
            skPoint(sketch, "E59.0.1.30", {"position": v(0, -7.5) * mm});
            skLineSegment(sketch, "E59.0.1.31", {"start": v(118, -1.5) * mm, "end": v(118, -13.5) * mm});
            skLineSegment(sketch, "E59.0.1.32", {"start": v(-12, -16.5) * mm, "end": v(14.5, -16.5) * mm, "construction": true});
            skLineSegment(sketch, "E59.0.1.33", {"start": v(65, -1.5) * mm, "end": v(65, -13.5) * mm});
            skPoint(sketch, "E59.0.1.34", {"position": v(-53, -7.5) * mm});
            skPoint(sketch, "E59.0.1.36", {"position": v(106, -7.5) * mm});
            skPoint(sketch, "E59.0.1.37", {"position": v(53, -7.5) * mm});
            skPoint(sketch, "E59.0.1.38", {"position": v(132.5, -7.5) * mm});
            skPoint(sketch, "E59.0.1.40", {"position": v(144.5, -16.5) * mm});
            skPoint(sketch, "E59.0.1.42", {"position": v(79.5, -7.5) * mm});
            skPoint(sketch, "E59.0.1.43", {"position": v(120.5, -16.5) * mm});
            skPoint(sketch, "E59.0.1.44", {"position": v(-120.5, -16.5) * mm});
            skLineSegment(sketch, "E59.0.1.46", {"start": v(-62, 1.5) * mm, "end": v(-44, 1.5) * mm});
            skLineSegment(sketch, "E59.0.1.47", {"start": v(-115, 1.5) * mm, "end": v(-97, 1.5) * mm});
            skPoint(sketch, "E59.0.1.48", {"position": v(91.5, -16.5) * mm});
            skLineSegment(sketch, "E59.0.1.49", {"start": v(-9, 1.5) * mm, "end": v(9, 1.5) * mm});
            skPoint(sketch, "E59.0.1.51", {"position": v(-144.5, -16.5) * mm});
            skLineSegment(sketch, "E59.0.1.53", {"start": v(17.5, -16.5) * mm, "end": v(35.5, -16.5) * mm});
            skPoint(sketch, "E59.0.1.54", {"position": v(-67.5, -16.5) * mm});
            skPoint(sketch, "E59.0.1.55", {"position": v(26.5, -7.5) * mm});
            skPoint(sketch, "E59.0.1.56", {"position": v(67.5, -16.5) * mm});
            skLineSegment(sketch, "E59.0.1.57", {"start": v(-144.5, -16.5) * mm, "end": v(-119.5, -16.5) * mm, "construction": true});
            skPoint(sketch, "E59.0.1.59", {"position": v(-26.5, -7.5) * mm});
            skPoint(sketch, "E59.0.1.62", {"position": v(-14.5, -16.5) * mm});
            skPoint(sketch, "E59.0.1.63", {"position": v(14.5, -16.5) * mm});
            skPoint(sketch, "E59.0.1.64", {"position": v(-79.5, -7.5) * mm});
            skLineSegment(sketch, "E59.0.1.65", {"start": v(-94, -1.5) * mm, "end": v(-94, -13.5) * mm});
            skLineSegment(sketch, "E59.0.1.66", {"start": v(-41, -1.5) * mm, "end": v(-41, -13.5) * mm});
            skLineSegment(sketch, "E59.0.1.67", {"start": v(120.5, -1.5) * mm, "end": v(120.5, -13.5) * mm});
            skLineSegment(sketch, "E59.0.1.68", {"start": v(67.5, -1.5) * mm, "end": v(67.5, -13.5) * mm});
            skLineSegment(sketch, "E59.0.1.69", {"start": v(-12, -16.5) * mm, "end": v(-38.5, -16.5) * mm, "construction": true});
            skLineSegment(sketch, "E59.0.1.72", {"start": v(17.5, 1.5) * mm, "end": v(35.5, 1.5) * mm});
            skLineSegment(sketch, "E59.0.1.73", {"start": v(-65, -1.5) * mm, "end": v(-65, -13.5) * mm});
            skLineSegment(sketch, "E59.0.1.74", {"start": v(123.5, 1.5) * mm, "end": v(141.5, 1.5) * mm});
            skLineSegment(sketch, "E59.0.1.75", {"start": v(70.5, 1.5) * mm, "end": v(88.5, 1.5) * mm});
            skLineSegment(sketch, "E59.0.1.76", {"start": v(91.5, -1.5) * mm, "end": v(91.5, -13.5) * mm});
            skLineSegment(sketch, "E59.0.1.77", {"start": v(70.5, -16.5) * mm, "end": v(88.5, -16.5) * mm});
            skLineSegment(sketch, "E59.0.1.78", {"start": v(123.5, -16.5) * mm, "end": v(141.5, -16.5) * mm});
            skLineSegment(sketch, "E59.0.1.79", {"start": v(-62, -16.5) * mm, "end": v(-44, -16.5) * mm});
            skLineSegment(sketch, "E59.0.1.80", {"start": v(-115, -16.5) * mm, "end": v(-97, -16.5) * mm});
            skPoint(sketch, "E59.0.1.81", {"position": v(-38.5, -16.5) * mm});
            skPoint(sketch, "E59.0.1.85", {"position": v(-132.5, -7.5) * mm});
            skPoint(sketch, "E59.0.1.86", {"position": v(-12, -16.5) * mm});
            skPoint(sketch, "E59.0.1.88", {"position": v(38.5, -16.5) * mm});
            skPoint(sketch, "E59.0.1.89", {"position": v(-91.5, -16.5) * mm});
            skLineSegment(sketch, "E59.0.1.90", {"start": v(14.5, -1.5) * mm, "end": v(14.5, -13.5) * mm});
            skLineSegment(sketch, "E59.0.1.91", {"start": v(38.5, -1.5) * mm, "end": v(38.5, -13.5) * mm});
            skPoint(sketch, "E59.0.1.93", {"position": v(12, -16.5) * mm});
            skLineSegment(sketch, "E59.0.1.96", {"start": v(-141.5, -16.5) * mm, "end": v(-123.5, -16.5) * mm});
            skLineSegment(sketch, "E59.0.1.97", {"start": v(-35.5, -16.5) * mm, "end": v(-17.5, -16.5) * mm});
            skLineSegment(sketch, "E59.0.1.98", {"start": v(-144.5, -1.5) * mm, "end": v(-144.5, -13.5) * mm});
            skLineSegment(sketch, "E59.0.1.99", {"start": v(-120.5, -1.5) * mm, "end": v(-120.5, -13.5) * mm});
            skLineSegment(sketch, "E59.0.1.100", {"start": v(-9, -16.5) * mm, "end": v(9, -16.5) * mm});
            skLineSegment(sketch, "E59.0.1.101", {"start": v(-118, -1.5) * mm, "end": v(-118, -13.5) * mm});
            skLineSegment(sketch, "E59.0.1.102", {"start": v(144.5, -1.5) * mm, "end": v(144.5, -13.5) * mm});
            skArc(sketch, "E59.0.1.103", {"start": v(-120.5, -1.5) * mm, "mid": v(-121.38, 0.62) * mm, "end": v(-123.5, 1.5) * mm});
            skArc(sketch, "E59.0.1.104", {"start": v(118, -1.5) * mm, "mid": v(117.12, 0.62) * mm, "end": v(115, 1.5) * mm});
            skArc(sketch, "E59.0.1.105", {"start": v(-14.5, -1.5) * mm, "mid": v(-15.38, 0.62) * mm, "end": v(-17.5, 1.5) * mm});
            skArc(sketch, "E59.0.1.106", {"start": v(41, -13.5) * mm, "mid": v(41.88, -15.62) * mm, "end": v(44, -16.5) * mm});
            skArc(sketch, "E59.0.1.107", {"start": v(94, -13.5) * mm, "mid": v(94.88, -15.62) * mm, "end": v(97, -16.5) * mm});
            skArc(sketch, "E59.0.1.108", {"start": v(62, -16.5) * mm, "mid": v(64.12, -15.62) * mm, "end": v(65, -13.5) * mm});
            skArc(sketch, "E59.0.1.109", {"start": v(115, -16.5) * mm, "mid": v(117.12, -15.62) * mm, "end": v(118, -13.5) * mm});
            skArc(sketch, "E59.0.1.110", {"start": v(-65, -13.5) * mm, "mid": v(-64.12, -15.62) * mm, "end": v(-62, -16.5) * mm});
            skArc(sketch, "E59.0.1.111", {"start": v(-118, -13.5) * mm, "mid": v(-117.12, -15.62) * mm, "end": v(-115, -16.5) * mm});
            skArc(sketch, "E59.0.1.112", {"start": v(70.5, 1.5) * mm, "mid": v(68.38, 0.62) * mm, "end": v(67.5, -1.5) * mm});
            skArc(sketch, "E59.0.1.113", {"start": v(-115, 1.5) * mm, "mid": v(-117.12, 0.62) * mm, "end": v(-118, -1.5) * mm});
            skArc(sketch, "E59.0.1.114", {"start": v(91.5, -1.5) * mm, "mid": v(90.62, 0.62) * mm, "end": v(88.5, 1.5) * mm});
            skArc(sketch, "E59.0.1.115", {"start": v(144.5, -1.5) * mm, "mid": v(143.62, 0.62) * mm, "end": v(141.5, 1.5) * mm});
            skArc(sketch, "E59.0.1.116", {"start": v(-94, -1.5) * mm, "mid": v(-94.88, 0.62) * mm, "end": v(-97, 1.5) * mm});
            skArc(sketch, "E59.0.1.117", {"start": v(38.5, -1.5) * mm, "mid": v(37.62, 0.62) * mm, "end": v(35.5, 1.5) * mm});
            skArc(sketch, "E59.0.1.118", {"start": v(88.5, -16.5) * mm, "mid": v(90.62, -15.62) * mm, "end": v(91.5, -13.5) * mm});
            skArc(sketch, "E59.0.1.119", {"start": v(35.5, -16.5) * mm, "mid": v(37.62, -15.62) * mm, "end": v(38.5, -13.5) * mm});
            skArc(sketch, "E59.0.1.120", {"start": v(-38.5, -13.5) * mm, "mid": v(-37.62, -15.62) * mm, "end": v(-35.5, -16.5) * mm});
            skArc(sketch, "E59.0.1.121", {"start": v(-91.5, -13.5) * mm, "mid": v(-90.62, -15.62) * mm, "end": v(-88.5, -16.5) * mm});
            skArc(sketch, "E59.0.1.122", {"start": v(-88.5, 1.5) * mm, "mid": v(-90.62, 0.62) * mm, "end": v(-91.5, -1.5) * mm});
            skArc(sketch, "E59.0.1.123", {"start": v(97, 1.5) * mm, "mid": v(94.88, 0.62) * mm, "end": v(94, -1.5) * mm});
            skArc(sketch, "E59.0.1.124", {"start": v(44, 1.5) * mm, "mid": v(41.88, 0.62) * mm, "end": v(41, -1.5) * mm});
            skArc(sketch, "E59.0.1.125", {"start": v(-141.5, 1.5) * mm, "mid": v(-143.62, 0.62) * mm, "end": v(-144.5, -1.5) * mm});
            skArc(sketch, "E59.0.1.126", {"start": v(65, -1.5) * mm, "mid": v(64.12, 0.62) * mm, "end": v(62, 1.5) * mm});
            skArc(sketch, "E59.0.1.127", {"start": v(-70.5, -16.5) * mm, "mid": v(-68.38, -15.62) * mm, "end": v(-67.5, -13.5) * mm});
            skArc(sketch, "E59.0.1.128", {"start": v(-17.5, -16.5) * mm, "mid": v(-15.38, -15.62) * mm, "end": v(-14.5, -13.5) * mm});
            skArc(sketch, "E59.0.1.129", {"start": v(-67.5, -1.5) * mm, "mid": v(-68.38, 0.62) * mm, "end": v(-70.5, 1.5) * mm});
            skArc(sketch, "E59.0.1.130", {"start": v(-12, -13.5) * mm, "mid": v(-11.12, -15.62) * mm, "end": v(-9, -16.5) * mm});
            skArc(sketch, "E59.0.1.131", {"start": v(-9, 1.5) * mm, "mid": v(-11.12, 0.62) * mm, "end": v(-12, -1.5) * mm});
            skArc(sketch, "E59.0.1.132", {"start": v(-123.5, -16.5) * mm, "mid": v(-121.38, -15.62) * mm, "end": v(-120.5, -13.5) * mm});
            skArc(sketch, "E59.0.1.133", {"start": v(123.5, 1.5) * mm, "mid": v(121.38, 0.62) * mm, "end": v(120.5, -1.5) * mm});
            skArc(sketch, "E59.0.1.134", {"start": v(-62, 1.5) * mm, "mid": v(-64.12, 0.62) * mm, "end": v(-65, -1.5) * mm});
            skArc(sketch, "E59.0.1.135", {"start": v(17.5, 1.5) * mm, "mid": v(15.38, 0.62) * mm, "end": v(14.5, -1.5) * mm});
            skArc(sketch, "E59.0.1.136", {"start": v(-41, -1.5) * mm, "mid": v(-41.88, 0.62) * mm, "end": v(-44, 1.5) * mm});
            skArc(sketch, "E59.0.1.137", {"start": v(141.5, -16.5) * mm, "mid": v(143.62, -15.62) * mm, "end": v(144.5, -13.5) * mm});
            skArc(sketch, "E59.0.1.138", {"start": v(-44, -16.5) * mm, "mid": v(-41.88, -15.62) * mm, "end": v(-41, -13.5) * mm});
            skArc(sketch, "E59.0.1.139", {"start": v(-97, -16.5) * mm, "mid": v(-94.88, -15.62) * mm, "end": v(-94, -13.5) * mm});
            skArc(sketch, "E59.0.1.140", {"start": v(67.5, -13.5) * mm, "mid": v(68.38, -15.62) * mm, "end": v(70.5, -16.5) * mm});
            skArc(sketch, "E59.0.1.141", {"start": v(120.5, -13.5) * mm, "mid": v(121.38, -15.62) * mm, "end": v(123.5, -16.5) * mm});
            skArc(sketch, "E59.0.1.142", {"start": v(14.5, -13.5) * mm, "mid": v(15.38, -15.62) * mm, "end": v(17.5, -16.5) * mm});
            skArc(sketch, "E59.0.1.143", {"start": v(-35.5, 1.5) * mm, "mid": v(-37.62, 0.62) * mm, "end": v(-38.5, -1.5) * mm});
            skArc(sketch, "E59.0.1.144", {"start": v(-144.5, -13.5) * mm, "mid": v(-143.62, -15.62) * mm, "end": v(-141.5, -16.5) * mm});
            skArc(sketch, "E59.0.1.145", {"start": v(9, -16.5) * mm, "mid": v(11.12, -15.62) * mm, "end": v(12, -13.5) * mm});
            skArc(sketch, "E59.0.1.146", {"start": v(12, -1.5) * mm, "mid": v(11.12, 0.62) * mm, "end": v(9, 1.5) * mm});
            skPoint(sketch, "E59.0.2.0", {"position": v(118, -37) * mm});
            skPoint(sketch, "E59.0.2.1", {"position": v(94, -37) * mm});
            skLineSegment(sketch, "E59.0.2.2", {"start": v(-12, -22) * mm, "end": v(-12, -34) * mm});
            skLineSegment(sketch, "E59.0.2.3", {"start": v(12, -22) * mm, "end": v(12, -34) * mm});
            skPoint(sketch, "E59.0.2.4", {"position": v(-14.5, -16.5) * mm});
            skLineSegment(sketch, "E59.0.2.5", {"start": v(-88.5, -19) * mm, "end": v(-70.5, -19) * mm});
            skLineSegment(sketch, "E59.0.2.6", {"start": v(-141.5, -19) * mm, "end": v(-123.5, -19) * mm});
            skLineSegment(sketch, "E59.0.2.7", {"start": v(-35.5, -19) * mm, "end": v(-17.5, -19) * mm});
            skPoint(sketch, "E59.0.2.8", {"position": v(-118, -37) * mm});
            skPoint(sketch, "E59.0.2.9", {"position": v(65, -37) * mm});
            skPoint(sketch, "E59.0.2.10", {"position": v(-41, -16.5) * mm});
            skPoint(sketch, "E59.0.2.11", {"position": v(-120.5, -16.5) * mm});
            skLineSegment(sketch, "E59.0.2.12", {"start": v(-88.5, -37) * mm, "end": v(-70.5, -37) * mm});
            skLineSegment(sketch, "E59.0.2.13", {"start": v(44, -37) * mm, "end": v(62, -37) * mm});
            skLineSegment(sketch, "E59.0.2.14", {"start": v(97, -37) * mm, "end": v(115, -37) * mm});
            skPoint(sketch, "E59.0.2.15", {"position": v(-41, -37) * mm});
            skPoint(sketch, "E59.0.2.16", {"position": v(-106, -28) * mm});
            skPoint(sketch, "E59.0.2.17", {"position": v(41, -37) * mm});
            skLineSegment(sketch, "E59.0.2.18", {"start": v(-91.5, -22) * mm, "end": v(-91.5, -34) * mm});
            skPoint(sketch, "E59.0.2.19", {"position": v(41, -16.5) * mm});
            skPoint(sketch, "E59.0.2.20", {"position": v(14.5, -16.5) * mm});
            skLineSegment(sketch, "E59.0.2.21", {"start": v(44, -19) * mm, "end": v(62, -19) * mm});
            skLineSegment(sketch, "E59.0.2.22", {"start": v(97, -19) * mm, "end": v(115, -19) * mm});
            skLineSegment(sketch, "E59.0.2.23", {"start": v(-38.5, -22) * mm, "end": v(-38.5, -34) * mm});
            skPoint(sketch, "E59.0.2.24", {"position": v(-65, -37) * mm});
            skLineSegment(sketch, "E59.0.2.25", {"start": v(-67.5, -22) * mm, "end": v(-67.5, -34) * mm});
            skLineSegment(sketch, "E59.0.2.26", {"start": v(41, -22) * mm, "end": v(41, -34) * mm});
            skLineSegment(sketch, "E59.0.2.27", {"start": v(94, -22) * mm, "end": v(94, -34) * mm});
            skLineSegment(sketch, "E59.0.2.28", {"start": v(-14.5, -22) * mm, "end": v(-14.5, -34) * mm});
            skPoint(sketch, "E59.0.2.29", {"position": v(-94, -37) * mm});
            skPoint(sketch, "E59.0.2.30", {"position": v(0, -28) * mm});
            skLineSegment(sketch, "E59.0.2.31", {"start": v(118, -22) * mm, "end": v(118, -34) * mm});
            skLineSegment(sketch, "E59.0.2.32", {"start": v(-12, -37) * mm, "end": v(14.5, -37) * mm, "construction": true});
            skLineSegment(sketch, "E59.0.2.33", {"start": v(65, -22) * mm, "end": v(65, -34) * mm});
            skPoint(sketch, "E59.0.2.34", {"position": v(-53, -28) * mm});
            skPoint(sketch, "E59.0.2.35", {"position": v(144.5, -16.5) * mm});
            skPoint(sketch, "E59.0.2.36", {"position": v(106, -28) * mm});
            skPoint(sketch, "E59.0.2.37", {"position": v(53, -28) * mm});
            skPoint(sketch, "E59.0.2.38", {"position": v(132.5, -28) * mm});
            skPoint(sketch, "E59.0.2.39", {"position": v(-38.5, -16.5) * mm});
            skPoint(sketch, "E59.0.2.40", {"position": v(144.5, -37) * mm});
            skPoint(sketch, "E59.0.2.41", {"position": v(-118, -16.5) * mm});
            skPoint(sketch, "E59.0.2.42", {"position": v(79.5, -28) * mm});
            skPoint(sketch, "E59.0.2.43", {"position": v(120.5, -37) * mm});
            skPoint(sketch, "E59.0.2.44", {"position": v(-120.5, -37) * mm});
            skPoint(sketch, "E59.0.2.45", {"position": v(65, -16.5) * mm});
            skLineSegment(sketch, "E59.0.2.46", {"start": v(-62, -19) * mm, "end": v(-44, -19) * mm});
            skLineSegment(sketch, "E59.0.2.47", {"start": v(-115, -19) * mm, "end": v(-97, -19) * mm});
            skPoint(sketch, "E59.0.2.48", {"position": v(91.5, -37) * mm});
            skLineSegment(sketch, "E59.0.2.49", {"start": v(-9, -19) * mm, "end": v(9, -19) * mm});
            skPoint(sketch, "E59.0.2.51", {"position": v(-144.5, -37) * mm});
            skPoint(sketch, "E59.0.2.52", {"position": v(94, -16.5) * mm});
            skLineSegment(sketch, "E59.0.2.53", {"start": v(17.5, -37) * mm, "end": v(35.5, -37) * mm});
            skPoint(sketch, "E59.0.2.54", {"position": v(-67.5, -37) * mm});
            skPoint(sketch, "E59.0.2.55", {"position": v(26.5, -28) * mm});
            skPoint(sketch, "E59.0.2.56", {"position": v(67.5, -37) * mm});
            skLineSegment(sketch, "E59.0.2.57", {"start": v(-144.5, -37) * mm, "end": v(-119.5, -37) * mm, "construction": true});
            skPoint(sketch, "E59.0.2.58", {"position": v(120.5, -16.5) * mm});
            skPoint(sketch, "E59.0.2.59", {"position": v(-26.5, -28) * mm});
            skPoint(sketch, "E59.0.2.60", {"position": v(12, -16.5) * mm});
            skPoint(sketch, "E59.0.2.61", {"position": v(-144.5, -16.5) * mm});
            skPoint(sketch, "E59.0.2.62", {"position": v(-14.5, -37) * mm});
            skPoint(sketch, "E59.0.2.63", {"position": v(14.5, -37) * mm});
            skPoint(sketch, "E59.0.2.64", {"position": v(-79.5, -28) * mm});
            skLineSegment(sketch, "E59.0.2.65", {"start": v(-94, -22) * mm, "end": v(-94, -34) * mm});
            skLineSegment(sketch, "E59.0.2.66", {"start": v(-41, -22) * mm, "end": v(-41, -34) * mm});
            skLineSegment(sketch, "E59.0.2.67", {"start": v(120.5, -22) * mm, "end": v(120.5, -34) * mm});
            skLineSegment(sketch, "E59.0.2.68", {"start": v(67.5, -22) * mm, "end": v(67.5, -34) * mm});
            skLineSegment(sketch, "E59.0.2.69", {"start": v(-12, -37) * mm, "end": v(-38.5, -37) * mm, "construction": true});
            skPoint(sketch, "E59.0.2.70", {"position": v(-94, -16.5) * mm});
            skPoint(sketch, "E59.0.2.71", {"position": v(38.5, -16.5) * mm});
            skLineSegment(sketch, "E59.0.2.72", {"start": v(17.5, -19) * mm, "end": v(35.5, -19) * mm});
            skLineSegment(sketch, "E59.0.2.73", {"start": v(-65, -22) * mm, "end": v(-65, -34) * mm});
            skLineSegment(sketch, "E59.0.2.74", {"start": v(123.5, -19) * mm, "end": v(141.5, -19) * mm});
            skLineSegment(sketch, "E59.0.2.75", {"start": v(70.5, -19) * mm, "end": v(88.5, -19) * mm});
            skLineSegment(sketch, "E59.0.2.76", {"start": v(91.5, -22) * mm, "end": v(91.5, -34) * mm});
            skLineSegment(sketch, "E59.0.2.77", {"start": v(70.5, -37) * mm, "end": v(88.5, -37) * mm});
            skLineSegment(sketch, "E59.0.2.78", {"start": v(123.5, -37) * mm, "end": v(141.5, -37) * mm});
            skLineSegment(sketch, "E59.0.2.79", {"start": v(-62, -37) * mm, "end": v(-44, -37) * mm});
            skLineSegment(sketch, "E59.0.2.80", {"start": v(-115, -37) * mm, "end": v(-97, -37) * mm});
            skPoint(sketch, "E59.0.2.81", {"position": v(-38.5, -37) * mm});
            skPoint(sketch, "E59.0.2.82", {"position": v(-12, -16.5) * mm});
            skPoint(sketch, "E59.0.2.83", {"position": v(-91.5, -16.5) * mm});
            skPoint(sketch, "E59.0.2.84", {"position": v(118, -16.5) * mm});
            skPoint(sketch, "E59.0.2.85", {"position": v(-132.5, -28) * mm});
            skPoint(sketch, "E59.0.2.86", {"position": v(-12, -37) * mm});
            skPoint(sketch, "E59.0.2.87", {"position": v(67.5, -16.5) * mm});
            skPoint(sketch, "E59.0.2.88", {"position": v(38.5, -37) * mm});
            skPoint(sketch, "E59.0.2.89", {"position": v(-91.5, -37) * mm});
            skLineSegment(sketch, "E59.0.2.90", {"start": v(14.5, -22) * mm, "end": v(14.5, -34) * mm});
            skLineSegment(sketch, "E59.0.2.91", {"start": v(38.5, -22) * mm, "end": v(38.5, -34) * mm});
            skPoint(sketch, "E59.0.2.92", {"position": v(-67.5, -16.5) * mm});
            skPoint(sketch, "E59.0.2.93", {"position": v(12, -37) * mm});
            skPoint(sketch, "E59.0.2.94", {"position": v(-65, -16.5) * mm});
            skPoint(sketch, "E59.0.2.95", {"position": v(91.5, -16.5) * mm});
            skLineSegment(sketch, "E59.0.2.96", {"start": v(-141.5, -37) * mm, "end": v(-123.5, -37) * mm});
            skLineSegment(sketch, "E59.0.2.97", {"start": v(-35.5, -37) * mm, "end": v(-17.5, -37) * mm});
            skLineSegment(sketch, "E59.0.2.98", {"start": v(-144.5, -22) * mm, "end": v(-144.5, -34) * mm});
            skLineSegment(sketch, "E59.0.2.99", {"start": v(-120.5, -22) * mm, "end": v(-120.5, -34) * mm});
            skLineSegment(sketch, "E59.0.2.100", {"start": v(-9, -37) * mm, "end": v(9, -37) * mm});
            skLineSegment(sketch, "E59.0.2.101", {"start": v(-118, -22) * mm, "end": v(-118, -34) * mm});
            skLineSegment(sketch, "E59.0.2.102", {"start": v(144.5, -22) * mm, "end": v(144.5, -34) * mm});
            skArc(sketch, "E59.0.2.103", {"start": v(-120.5, -22) * mm, "mid": v(-121.38, -19.88) * mm, "end": v(-123.5, -19) * mm});
            skArc(sketch, "E59.0.2.104", {"start": v(118, -22) * mm, "mid": v(117.12, -19.88) * mm, "end": v(115, -19) * mm});
            skArc(sketch, "E59.0.2.105", {"start": v(-14.5, -22) * mm, "mid": v(-15.38, -19.88) * mm, "end": v(-17.5, -19) * mm});
            skArc(sketch, "E59.0.2.106", {"start": v(41, -34) * mm, "mid": v(41.88, -36.12) * mm, "end": v(44, -37) * mm});
            skArc(sketch, "E59.0.2.107", {"start": v(94, -34) * mm, "mid": v(94.88, -36.12) * mm, "end": v(97, -37) * mm});
            skArc(sketch, "E59.0.2.108", {"start": v(62, -37) * mm, "mid": v(64.12, -36.12) * mm, "end": v(65, -34) * mm});
            skArc(sketch, "E59.0.2.109", {"start": v(115, -37) * mm, "mid": v(117.12, -36.12) * mm, "end": v(118, -34) * mm});
            skArc(sketch, "E59.0.2.110", {"start": v(-65, -34) * mm, "mid": v(-64.12, -36.12) * mm, "end": v(-62, -37) * mm});
            skArc(sketch, "E59.0.2.111", {"start": v(-118, -34) * mm, "mid": v(-117.12, -36.12) * mm, "end": v(-115, -37) * mm});
            skArc(sketch, "E59.0.2.112", {"start": v(70.5, -19) * mm, "mid": v(68.38, -19.88) * mm, "end": v(67.5, -22) * mm});
            skArc(sketch, "E59.0.2.113", {"start": v(-115, -19) * mm, "mid": v(-117.12, -19.88) * mm, "end": v(-118, -22) * mm});
            skArc(sketch, "E59.0.2.114", {"start": v(91.5, -22) * mm, "mid": v(90.62, -19.88) * mm, "end": v(88.5, -19) * mm});
            skArc(sketch, "E59.0.2.115", {"start": v(144.5, -22) * mm, "mid": v(143.62, -19.88) * mm, "end": v(141.5, -19) * mm});
            skArc(sketch, "E59.0.2.116", {"start": v(-94, -22) * mm, "mid": v(-94.88, -19.88) * mm, "end": v(-97, -19) * mm});
            skArc(sketch, "E59.0.2.117", {"start": v(38.5, -22) * mm, "mid": v(37.62, -19.88) * mm, "end": v(35.5, -19) * mm});
            skArc(sketch, "E59.0.2.118", {"start": v(88.5, -37) * mm, "mid": v(90.62, -36.12) * mm, "end": v(91.5, -34) * mm});
            skArc(sketch, "E59.0.2.119", {"start": v(35.5, -37) * mm, "mid": v(37.62, -36.12) * mm, "end": v(38.5, -34) * mm});
            skArc(sketch, "E59.0.2.120", {"start": v(-38.5, -34) * mm, "mid": v(-37.62, -36.12) * mm, "end": v(-35.5, -37) * mm});
            skArc(sketch, "E59.0.2.121", {"start": v(-91.5, -34) * mm, "mid": v(-90.62, -36.12) * mm, "end": v(-88.5, -37) * mm});
            skArc(sketch, "E59.0.2.122", {"start": v(-88.5, -19) * mm, "mid": v(-90.62, -19.88) * mm, "end": v(-91.5, -22) * mm});
            skArc(sketch, "E59.0.2.123", {"start": v(97, -19) * mm, "mid": v(94.88, -19.88) * mm, "end": v(94, -22) * mm});
            skArc(sketch, "E59.0.2.124", {"start": v(44, -19) * mm, "mid": v(41.88, -19.88) * mm, "end": v(41, -22) * mm});
            skArc(sketch, "E59.0.2.125", {"start": v(-141.5, -19) * mm, "mid": v(-143.62, -19.88) * mm, "end": v(-144.5, -22) * mm});
            skArc(sketch, "E59.0.2.126", {"start": v(65, -22) * mm, "mid": v(64.12, -19.88) * mm, "end": v(62, -19) * mm});
            skArc(sketch, "E59.0.2.127", {"start": v(-70.5, -37) * mm, "mid": v(-68.38, -36.12) * mm, "end": v(-67.5, -34) * mm});
            skArc(sketch, "E59.0.2.128", {"start": v(-17.5, -37) * mm, "mid": v(-15.38, -36.12) * mm, "end": v(-14.5, -34) * mm});
            skArc(sketch, "E59.0.2.129", {"start": v(-67.5, -22) * mm, "mid": v(-68.38, -19.88) * mm, "end": v(-70.5, -19) * mm});
            skArc(sketch, "E59.0.2.130", {"start": v(-12, -34) * mm, "mid": v(-11.12, -36.12) * mm, "end": v(-9, -37) * mm});
            skArc(sketch, "E59.0.2.131", {"start": v(-9, -19) * mm, "mid": v(-11.12, -19.88) * mm, "end": v(-12, -22) * mm});
            skArc(sketch, "E59.0.2.132", {"start": v(-123.5, -37) * mm, "mid": v(-121.38, -36.12) * mm, "end": v(-120.5, -34) * mm});
            skArc(sketch, "E59.0.2.133", {"start": v(123.5, -19) * mm, "mid": v(121.38, -19.88) * mm, "end": v(120.5, -22) * mm});
            skArc(sketch, "E59.0.2.134", {"start": v(-62, -19) * mm, "mid": v(-64.12, -19.88) * mm, "end": v(-65, -22) * mm});
            skArc(sketch, "E59.0.2.135", {"start": v(17.5, -19) * mm, "mid": v(15.38, -19.88) * mm, "end": v(14.5, -22) * mm});
            skArc(sketch, "E59.0.2.136", {"start": v(-41, -22) * mm, "mid": v(-41.88, -19.88) * mm, "end": v(-44, -19) * mm});
            skArc(sketch, "E59.0.2.137", {"start": v(141.5, -37) * mm, "mid": v(143.62, -36.12) * mm, "end": v(144.5, -34) * mm});
            skArc(sketch, "E59.0.2.138", {"start": v(-44, -37) * mm, "mid": v(-41.88, -36.12) * mm, "end": v(-41, -34) * mm});
            skArc(sketch, "E59.0.2.139", {"start": v(-97, -37) * mm, "mid": v(-94.88, -36.12) * mm, "end": v(-94, -34) * mm});
            skArc(sketch, "E59.0.2.140", {"start": v(67.5, -34) * mm, "mid": v(68.38, -36.12) * mm, "end": v(70.5, -37) * mm});
            skArc(sketch, "E59.0.2.141", {"start": v(120.5, -34) * mm, "mid": v(121.38, -36.12) * mm, "end": v(123.5, -37) * mm});
            skArc(sketch, "E59.0.2.142", {"start": v(14.5, -34) * mm, "mid": v(15.38, -36.12) * mm, "end": v(17.5, -37) * mm});
            skArc(sketch, "E59.0.2.143", {"start": v(-35.5, -19) * mm, "mid": v(-37.62, -19.88) * mm, "end": v(-38.5, -22) * mm});
            skArc(sketch, "E59.0.2.144", {"start": v(-144.5, -34) * mm, "mid": v(-143.62, -36.12) * mm, "end": v(-141.5, -37) * mm});
            skArc(sketch, "E59.0.2.145", {"start": v(9, -37) * mm, "mid": v(11.12, -36.12) * mm, "end": v(12, -34) * mm});
            skArc(sketch, "E59.0.2.146", {"start": v(12, -22) * mm, "mid": v(11.12, -19.88) * mm, "end": v(9, -19) * mm});
            skPoint(sketch, "E59.0.3.0", {"position": v(118, -57.5) * mm});
            skPoint(sketch, "E59.0.3.1", {"position": v(94, -57.5) * mm});
            skLineSegment(sketch, "E59.0.3.2", {"start": v(-12, -42.5) * mm, "end": v(-12, -54.5) * mm});
            skLineSegment(sketch, "E59.0.3.3", {"start": v(12, -42.5) * mm, "end": v(12, -54.5) * mm});
            skPoint(sketch, "E59.0.3.4", {"position": v(-14.5, -37) * mm});
            skLineSegment(sketch, "E59.0.3.5", {"start": v(-88.5, -39.5) * mm, "end": v(-70.5, -39.5) * mm});
            skLineSegment(sketch, "E59.0.3.6", {"start": v(-141.5, -39.5) * mm, "end": v(-123.5, -39.5) * mm});
            skLineSegment(sketch, "E59.0.3.7", {"start": v(-35.5, -39.5) * mm, "end": v(-17.5, -39.5) * mm});
            skPoint(sketch, "E59.0.3.8", {"position": v(-118, -57.5) * mm});
            skPoint(sketch, "E59.0.3.9", {"position": v(65, -57.5) * mm});
            skPoint(sketch, "E59.0.3.10", {"position": v(-41, -37) * mm});
            skPoint(sketch, "E59.0.3.11", {"position": v(-120.5, -37) * mm});
            skLineSegment(sketch, "E59.0.3.12", {"start": v(-88.5, -57.5) * mm, "end": v(-70.5, -57.5) * mm});
            skLineSegment(sketch, "E59.0.3.13", {"start": v(44, -57.5) * mm, "end": v(62, -57.5) * mm});
            skLineSegment(sketch, "E59.0.3.14", {"start": v(97, -57.5) * mm, "end": v(115, -57.5) * mm});
            skPoint(sketch, "E59.0.3.15", {"position": v(-41, -57.5) * mm});
            skPoint(sketch, "E59.0.3.16", {"position": v(-106, -48.5) * mm});
            skPoint(sketch, "E59.0.3.17", {"position": v(41, -57.5) * mm});
            skLineSegment(sketch, "E59.0.3.18", {"start": v(-91.5, -42.5) * mm, "end": v(-91.5, -54.5) * mm});
            skPoint(sketch, "E59.0.3.19", {"position": v(41, -37) * mm});
            skPoint(sketch, "E59.0.3.20", {"position": v(14.5, -37) * mm});
            skLineSegment(sketch, "E59.0.3.21", {"start": v(44, -39.5) * mm, "end": v(62, -39.5) * mm});
            skLineSegment(sketch, "E59.0.3.22", {"start": v(97, -39.5) * mm, "end": v(115, -39.5) * mm});
            skLineSegment(sketch, "E59.0.3.23", {"start": v(-38.5, -42.5) * mm, "end": v(-38.5, -54.5) * mm});
            skPoint(sketch, "E59.0.3.24", {"position": v(-65, -57.5) * mm});
            skLineSegment(sketch, "E59.0.3.25", {"start": v(-67.5, -42.5) * mm, "end": v(-67.5, -54.5) * mm});
            skLineSegment(sketch, "E59.0.3.26", {"start": v(41, -42.5) * mm, "end": v(41, -54.5) * mm});
            skLineSegment(sketch, "E59.0.3.27", {"start": v(94, -42.5) * mm, "end": v(94, -54.5) * mm});
            skLineSegment(sketch, "E59.0.3.28", {"start": v(-14.5, -42.5) * mm, "end": v(-14.5, -54.5) * mm});
            skPoint(sketch, "E59.0.3.29", {"position": v(-94, -57.5) * mm});
            skPoint(sketch, "E59.0.3.30", {"position": v(0, -48.5) * mm});
            skLineSegment(sketch, "E59.0.3.31", {"start": v(118, -42.5) * mm, "end": v(118, -54.5) * mm});
            skLineSegment(sketch, "E59.0.3.32", {"start": v(-12, -57.5) * mm, "end": v(14.5, -57.5) * mm, "construction": true});
            skLineSegment(sketch, "E59.0.3.33", {"start": v(65, -42.5) * mm, "end": v(65, -54.5) * mm});
            skPoint(sketch, "E59.0.3.34", {"position": v(-53, -48.5) * mm});
            skPoint(sketch, "E59.0.3.35", {"position": v(144.5, -37) * mm});
            skPoint(sketch, "E59.0.3.36", {"position": v(106, -48.5) * mm});
            skPoint(sketch, "E59.0.3.37", {"position": v(53, -48.5) * mm});
            skPoint(sketch, "E59.0.3.38", {"position": v(132.5, -48.5) * mm});
            skPoint(sketch, "E59.0.3.39", {"position": v(-38.5, -37) * mm});
            skPoint(sketch, "E59.0.3.40", {"position": v(144.5, -57.5) * mm});
            skPoint(sketch, "E59.0.3.41", {"position": v(-118, -37) * mm});
            skPoint(sketch, "E59.0.3.42", {"position": v(79.5, -48.5) * mm});
            skPoint(sketch, "E59.0.3.43", {"position": v(120.5, -57.5) * mm});
            skPoint(sketch, "E59.0.3.44", {"position": v(-120.5, -57.5) * mm});
            skPoint(sketch, "E59.0.3.45", {"position": v(65, -37) * mm});
            skLineSegment(sketch, "E59.0.3.46", {"start": v(-62, -39.5) * mm, "end": v(-44, -39.5) * mm});
            skLineSegment(sketch, "E59.0.3.47", {"start": v(-115, -39.5) * mm, "end": v(-97, -39.5) * mm});
            skPoint(sketch, "E59.0.3.48", {"position": v(91.5, -57.5) * mm});
            skLineSegment(sketch, "E59.0.3.49", {"start": v(-9, -39.5) * mm, "end": v(9, -39.5) * mm});
            skPoint(sketch, "E59.0.3.51", {"position": v(-144.5, -57.5) * mm});
            skPoint(sketch, "E59.0.3.52", {"position": v(94, -37) * mm});
            skLineSegment(sketch, "E59.0.3.53", {"start": v(17.5, -57.5) * mm, "end": v(35.5, -57.5) * mm});
            skPoint(sketch, "E59.0.3.54", {"position": v(-67.5, -57.5) * mm});
            skPoint(sketch, "E59.0.3.55", {"position": v(26.5, -48.5) * mm});
            skPoint(sketch, "E59.0.3.56", {"position": v(67.5, -57.5) * mm});
            skLineSegment(sketch, "E59.0.3.57", {"start": v(-144.5, -57.5) * mm, "end": v(-119.5, -57.5) * mm, "construction": true});
            skPoint(sketch, "E59.0.3.58", {"position": v(120.5, -37) * mm});
            skPoint(sketch, "E59.0.3.59", {"position": v(-26.5, -48.5) * mm});
            skPoint(sketch, "E59.0.3.60", {"position": v(12, -37) * mm});
            skPoint(sketch, "E59.0.3.61", {"position": v(-144.5, -37) * mm});
            skPoint(sketch, "E59.0.3.62", {"position": v(-14.5, -57.5) * mm});
            skPoint(sketch, "E59.0.3.63", {"position": v(14.5, -57.5) * mm});
            skPoint(sketch, "E59.0.3.64", {"position": v(-79.5, -48.5) * mm});
            skLineSegment(sketch, "E59.0.3.65", {"start": v(-94, -42.5) * mm, "end": v(-94, -54.5) * mm});
            skLineSegment(sketch, "E59.0.3.66", {"start": v(-41, -42.5) * mm, "end": v(-41, -54.5) * mm});
            skLineSegment(sketch, "E59.0.3.67", {"start": v(120.5, -42.5) * mm, "end": v(120.5, -54.5) * mm});
            skLineSegment(sketch, "E59.0.3.68", {"start": v(67.5, -42.5) * mm, "end": v(67.5, -54.5) * mm});
            skLineSegment(sketch, "E59.0.3.69", {"start": v(-12, -57.5) * mm, "end": v(-38.5, -57.5) * mm, "construction": true});
            skPoint(sketch, "E59.0.3.70", {"position": v(-94, -37) * mm});
            skPoint(sketch, "E59.0.3.71", {"position": v(38.5, -37) * mm});
            skLineSegment(sketch, "E59.0.3.72", {"start": v(17.5, -39.5) * mm, "end": v(35.5, -39.5) * mm});
            skLineSegment(sketch, "E59.0.3.73", {"start": v(-65, -42.5) * mm, "end": v(-65, -54.5) * mm});
            skLineSegment(sketch, "E59.0.3.74", {"start": v(123.5, -39.5) * mm, "end": v(141.5, -39.5) * mm});
            skLineSegment(sketch, "E59.0.3.75", {"start": v(70.5, -39.5) * mm, "end": v(88.5, -39.5) * mm});
            skLineSegment(sketch, "E59.0.3.76", {"start": v(91.5, -42.5) * mm, "end": v(91.5, -54.5) * mm});
            skLineSegment(sketch, "E59.0.3.77", {"start": v(70.5, -57.5) * mm, "end": v(88.5, -57.5) * mm});
            skLineSegment(sketch, "E59.0.3.78", {"start": v(123.5, -57.5) * mm, "end": v(141.5, -57.5) * mm});
            skLineSegment(sketch, "E59.0.3.79", {"start": v(-62, -57.5) * mm, "end": v(-44, -57.5) * mm});
            skLineSegment(sketch, "E59.0.3.80", {"start": v(-115, -57.5) * mm, "end": v(-97, -57.5) * mm});
            skPoint(sketch, "E59.0.3.81", {"position": v(-38.5, -57.5) * mm});
            skPoint(sketch, "E59.0.3.82", {"position": v(-12, -37) * mm});
            skPoint(sketch, "E59.0.3.83", {"position": v(-91.5, -37) * mm});
            skPoint(sketch, "E59.0.3.84", {"position": v(118, -37) * mm});
            skPoint(sketch, "E59.0.3.85", {"position": v(-132.5, -48.5) * mm});
            skPoint(sketch, "E59.0.3.86", {"position": v(-12, -57.5) * mm});
            skPoint(sketch, "E59.0.3.87", {"position": v(67.5, -37) * mm});
            skPoint(sketch, "E59.0.3.88", {"position": v(38.5, -57.5) * mm});
            skPoint(sketch, "E59.0.3.89", {"position": v(-91.5, -57.5) * mm});
            skLineSegment(sketch, "E59.0.3.90", {"start": v(14.5, -42.5) * mm, "end": v(14.5, -54.5) * mm});
            skLineSegment(sketch, "E59.0.3.91", {"start": v(38.5, -42.5) * mm, "end": v(38.5, -54.5) * mm});
            skPoint(sketch, "E59.0.3.92", {"position": v(-67.5, -37) * mm});
            skPoint(sketch, "E59.0.3.93", {"position": v(12, -57.5) * mm});
            skPoint(sketch, "E59.0.3.94", {"position": v(-65, -37) * mm});
            skPoint(sketch, "E59.0.3.95", {"position": v(91.5, -37) * mm});
            skLineSegment(sketch, "E59.0.3.96", {"start": v(-141.5, -57.5) * mm, "end": v(-123.5, -57.5) * mm});
            skLineSegment(sketch, "E59.0.3.97", {"start": v(-35.5, -57.5) * mm, "end": v(-17.5, -57.5) * mm});
            skLineSegment(sketch, "E59.0.3.98", {"start": v(-144.5, -42.5) * mm, "end": v(-144.5, -54.5) * mm});
            skLineSegment(sketch, "E59.0.3.99", {"start": v(-120.5, -42.5) * mm, "end": v(-120.5, -54.5) * mm});
            skLineSegment(sketch, "E59.0.3.100", {"start": v(-9, -57.5) * mm, "end": v(9, -57.5) * mm});
            skLineSegment(sketch, "E59.0.3.101", {"start": v(-118, -42.5) * mm, "end": v(-118, -54.5) * mm});
            skLineSegment(sketch, "E59.0.3.102", {"start": v(144.5, -42.5) * mm, "end": v(144.5, -54.5) * mm});
            skArc(sketch, "E59.0.3.103", {"start": v(-120.5, -42.5) * mm, "mid": v(-121.38, -40.38) * mm, "end": v(-123.5, -39.5) * mm});
            skArc(sketch, "E59.0.3.104", {"start": v(118, -42.5) * mm, "mid": v(117.12, -40.38) * mm, "end": v(115, -39.5) * mm});
            skArc(sketch, "E59.0.3.105", {"start": v(-14.5, -42.5) * mm, "mid": v(-15.38, -40.38) * mm, "end": v(-17.5, -39.5) * mm});
            skArc(sketch, "E59.0.3.106", {"start": v(41, -54.5) * mm, "mid": v(41.88, -56.62) * mm, "end": v(44, -57.5) * mm});
            skArc(sketch, "E59.0.3.107", {"start": v(94, -54.5) * mm, "mid": v(94.88, -56.62) * mm, "end": v(97, -57.5) * mm});
            skArc(sketch, "E59.0.3.108", {"start": v(62, -57.5) * mm, "mid": v(64.12, -56.62) * mm, "end": v(65, -54.5) * mm});
            skArc(sketch, "E59.0.3.109", {"start": v(115, -57.5) * mm, "mid": v(117.12, -56.62) * mm, "end": v(118, -54.5) * mm});
            skArc(sketch, "E59.0.3.110", {"start": v(-65, -54.5) * mm, "mid": v(-64.12, -56.62) * mm, "end": v(-62, -57.5) * mm});
            skArc(sketch, "E59.0.3.111", {"start": v(-118, -54.5) * mm, "mid": v(-117.12, -56.62) * mm, "end": v(-115, -57.5) * mm});
            skArc(sketch, "E59.0.3.112", {"start": v(70.5, -39.5) * mm, "mid": v(68.38, -40.38) * mm, "end": v(67.5, -42.5) * mm});
            skArc(sketch, "E59.0.3.113", {"start": v(-115, -39.5) * mm, "mid": v(-117.12, -40.38) * mm, "end": v(-118, -42.5) * mm});
            skArc(sketch, "E59.0.3.114", {"start": v(91.5, -42.5) * mm, "mid": v(90.62, -40.38) * mm, "end": v(88.5, -39.5) * mm});
            skArc(sketch, "E59.0.3.115", {"start": v(144.5, -42.5) * mm, "mid": v(143.62, -40.38) * mm, "end": v(141.5, -39.5) * mm});
            skArc(sketch, "E59.0.3.116", {"start": v(-94, -42.5) * mm, "mid": v(-94.88, -40.38) * mm, "end": v(-97, -39.5) * mm});
            skArc(sketch, "E59.0.3.117", {"start": v(38.5, -42.5) * mm, "mid": v(37.62, -40.38) * mm, "end": v(35.5, -39.5) * mm});
            skArc(sketch, "E59.0.3.118", {"start": v(88.5, -57.5) * mm, "mid": v(90.62, -56.62) * mm, "end": v(91.5, -54.5) * mm});
            skArc(sketch, "E59.0.3.119", {"start": v(35.5, -57.5) * mm, "mid": v(37.62, -56.62) * mm, "end": v(38.5, -54.5) * mm});
            skArc(sketch, "E59.0.3.120", {"start": v(-38.5, -54.5) * mm, "mid": v(-37.62, -56.62) * mm, "end": v(-35.5, -57.5) * mm});
            skArc(sketch, "E59.0.3.121", {"start": v(-91.5, -54.5) * mm, "mid": v(-90.62, -56.62) * mm, "end": v(-88.5, -57.5) * mm});
            skArc(sketch, "E59.0.3.122", {"start": v(-88.5, -39.5) * mm, "mid": v(-90.62, -40.38) * mm, "end": v(-91.5, -42.5) * mm});
            skArc(sketch, "E59.0.3.123", {"start": v(97, -39.5) * mm, "mid": v(94.88, -40.38) * mm, "end": v(94, -42.5) * mm});
            skArc(sketch, "E59.0.3.124", {"start": v(44, -39.5) * mm, "mid": v(41.88, -40.38) * mm, "end": v(41, -42.5) * mm});
            skArc(sketch, "E59.0.3.125", {"start": v(-141.5, -39.5) * mm, "mid": v(-143.62, -40.38) * mm, "end": v(-144.5, -42.5) * mm});
            skArc(sketch, "E59.0.3.126", {"start": v(65, -42.5) * mm, "mid": v(64.12, -40.38) * mm, "end": v(62, -39.5) * mm});
            skArc(sketch, "E59.0.3.127", {"start": v(-70.5, -57.5) * mm, "mid": v(-68.38, -56.62) * mm, "end": v(-67.5, -54.5) * mm});
            skArc(sketch, "E59.0.3.128", {"start": v(-17.5, -57.5) * mm, "mid": v(-15.38, -56.62) * mm, "end": v(-14.5, -54.5) * mm});
            skArc(sketch, "E59.0.3.129", {"start": v(-67.5, -42.5) * mm, "mid": v(-68.38, -40.38) * mm, "end": v(-70.5, -39.5) * mm});
            skArc(sketch, "E59.0.3.130", {"start": v(-12, -54.5) * mm, "mid": v(-11.12, -56.62) * mm, "end": v(-9, -57.5) * mm});
            skArc(sketch, "E59.0.3.131", {"start": v(-9, -39.5) * mm, "mid": v(-11.12, -40.38) * mm, "end": v(-12, -42.5) * mm});
            skArc(sketch, "E59.0.3.132", {"start": v(-123.5, -57.5) * mm, "mid": v(-121.38, -56.62) * mm, "end": v(-120.5, -54.5) * mm});
            skArc(sketch, "E59.0.3.133", {"start": v(123.5, -39.5) * mm, "mid": v(121.38, -40.38) * mm, "end": v(120.5, -42.5) * mm});
            skArc(sketch, "E59.0.3.134", {"start": v(-62, -39.5) * mm, "mid": v(-64.12, -40.38) * mm, "end": v(-65, -42.5) * mm});
            skArc(sketch, "E59.0.3.135", {"start": v(17.5, -39.5) * mm, "mid": v(15.38, -40.38) * mm, "end": v(14.5, -42.5) * mm});
            skArc(sketch, "E59.0.3.136", {"start": v(-41, -42.5) * mm, "mid": v(-41.88, -40.38) * mm, "end": v(-44, -39.5) * mm});
            skArc(sketch, "E59.0.3.137", {"start": v(141.5, -57.5) * mm, "mid": v(143.62, -56.62) * mm, "end": v(144.5, -54.5) * mm});
            skArc(sketch, "E59.0.3.138", {"start": v(-44, -57.5) * mm, "mid": v(-41.88, -56.62) * mm, "end": v(-41, -54.5) * mm});
            skArc(sketch, "E59.0.3.139", {"start": v(-97, -57.5) * mm, "mid": v(-94.88, -56.62) * mm, "end": v(-94, -54.5) * mm});
            skArc(sketch, "E59.0.3.140", {"start": v(67.5, -54.5) * mm, "mid": v(68.38, -56.62) * mm, "end": v(70.5, -57.5) * mm});
            skArc(sketch, "E59.0.3.141", {"start": v(120.5, -54.5) * mm, "mid": v(121.38, -56.62) * mm, "end": v(123.5, -57.5) * mm});
            skArc(sketch, "E59.0.3.142", {"start": v(14.5, -54.5) * mm, "mid": v(15.38, -56.62) * mm, "end": v(17.5, -57.5) * mm});
            skArc(sketch, "E59.0.3.143", {"start": v(-35.5, -39.5) * mm, "mid": v(-37.62, -40.38) * mm, "end": v(-38.5, -42.5) * mm});
            skArc(sketch, "E59.0.3.144", {"start": v(-144.5, -54.5) * mm, "mid": v(-143.62, -56.62) * mm, "end": v(-141.5, -57.5) * mm});
            skArc(sketch, "E59.0.3.145", {"start": v(9, -57.5) * mm, "mid": v(11.12, -56.62) * mm, "end": v(12, -54.5) * mm});
            skArc(sketch, "E59.0.3.146", {"start": v(12, -42.5) * mm, "mid": v(11.12, -40.38) * mm, "end": v(9, -39.5) * mm});
            skLineSegment(sketch, "E59.direction2", {"start": v(-144.5, 4) * mm, "end": v(-144.5, -16.5) * mm, "construction": true});
            skLineSegment(sketch, "E60", {"start": v(-9, 22) * mm, "end": v(9, 22) * mm});
            skSolve(sketch);
        }
        {
            var Q0;
            Q0 = qSketchRegion(id + "F4", true);
            extrude(context, id + "F5", {"entities" : qUnion([Q0]), "operationType" : NewBodyOperationType.REMOVE, "oppositeDirection" : true, "depth" : 3 * mm});
        }
        {
            var Q0;
            Q0=makeQuery(id+"F1.opExtrude","CAP_FACE",FACE,{"disambiguationData":[OSD([sQuery(id+"F0.wireOp",EDGE,"E0.bottom"),sQuery(id+"F0.wireOp",EDGE,"E0.top"),sQuery(id+"F0.wireOp",EDGE,"E0.left"),sQuery(id+"F0.wireOp",EDGE,"E0.right"),sQuery(id+"F0.wireOp",EDGE,"E1.filletArc"),sQuery(id+"F0.wireOp",EDGE,"E2.filletArc"),sQuery(id+"F0.wireOp",EDGE,"E3.filletArc"),sQuery(id+"F0.wireOp",EDGE,"E4.filletArc")])],"isStart":false});
            var sketch = newSketch(context, id + "F6", { "sketchPlane" : qUnion([Q0])});
            skLineSegment(sketch, "E61", {"start": v(-139.5, -60) * mm, "end": v(139.5, -60) * mm});
            skLineSegment(sketch, "E62", {"start": v(144.5, -65) * mm, "end": v(144.5, -73) * mm});
            skLineSegment(sketch, "E63", {"start": v(139.5, -78) * mm, "end": v(-139.5, -78) * mm});
            skLineSegment(sketch, "E64", {"start": v(-144.5, -73) * mm, "end": v(-144.5, -65) * mm});
            skPoint(sketch, "E65.visualSharp", {"position": v(-144.5, -60) * mm});
            skArc(sketch, "E65.filletArc", {"start": v(-139.5, -60) * mm, "mid": v(-143.04, -61.46) * mm, "end": v(-144.5, -65) * mm});
            skPoint(sketch, "E66.visualSharp", {"position": v(-144.5, -78) * mm});
            skArc(sketch, "E66.filletArc", {"start": v(-144.5, -73) * mm, "mid": v(-143.04, -76.54) * mm, "end": v(-139.5, -78) * mm});
            skPoint(sketch, "E67.visualSharp", {"position": v(144.5, -78) * mm});
            skArc(sketch, "E67.filletArc", {"start": v(139.5, -78) * mm, "mid": v(143.04, -76.54) * mm, "end": v(144.5, -73) * mm});
            skPoint(sketch, "E68.visualSharp", {"position": v(144.5, -60) * mm});
            skArc(sketch, "E68.filletArc", {"start": v(144.5, -65) * mm, "mid": v(143.04, -61.46) * mm, "end": v(139.5, -60) * mm});
            skSolve(sketch);
        }
        {
            var Q0;
            Q0 = qSketchRegion(id + "F6", true);
            extrude(context, id + "F7", {"entities" : qUnion([Q0]), "operationType" : NewBodyOperationType.REMOVE, "oppositeDirection" : true, "depth" : 3 * mm});
        }
    });
